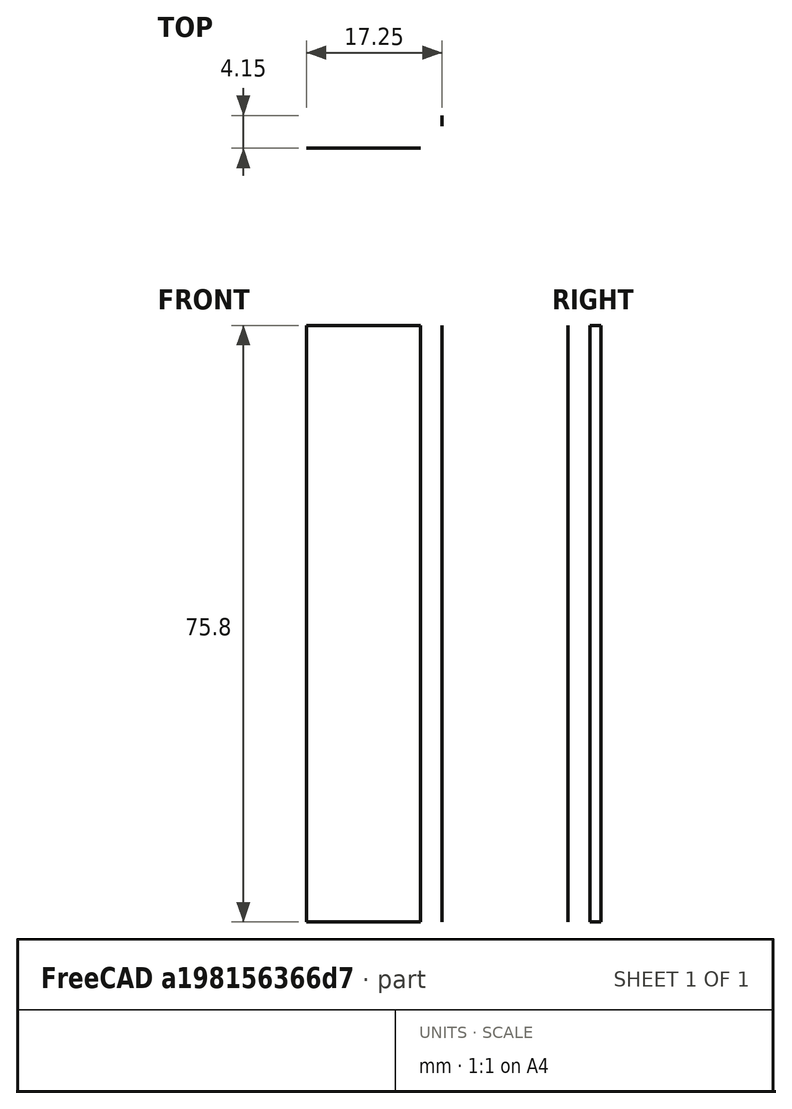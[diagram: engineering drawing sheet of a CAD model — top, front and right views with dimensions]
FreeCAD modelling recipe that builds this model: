
FCSTD DOCUMENT  (FreeCAD 2021.717R24301 +3842 (Git))
Label: Z-carriage
License: Creative Commons Attribution
LicenseURL: http://creativecommons.org/licenses/by/4.0/
objects: App::FeaturePython×34, Part::FeaturePython×25, App::Link×11
note: 24 computed .brp shape members not serialized (recipe doc carries the construction recipe); baked Part::Feature solids carry a one-line shape summary decoded from their .brp
EXTERNAL_REF file=parts/Spindle.FCStd obj=Assembly001
EXTERNAL_REF file=parts/HGH20CA.FCStd obj=Assembly
EXTERNAL_REF file=parts/HGH20CA.FCStd obj=Assembly001
EXTERNAL_REF file=parts/BallNut.FCStd obj=Assembly
EXTERNAL_REF file=parts/Z axis plates.FCStd obj=Assembly002
EXTERNAL_REF file=parts/Z axis plates.FCStd obj=Assembly001
EXTERNAL_REF file=parts/Z axis plates.FCStd obj=Assembly003
EXTERNAL_REF file=parts/Spindle.FCStd obj=Assembly002

FEATURE [App::Link] Link023  label="Spindle 0.8KW"
  AutoLinkLabel = true
  AutoPlacement = true
  LinkPlacement = pos=(255,-86.85,-102.5) rot=(0,0,-1;3.14159rad)
  LinkedObject = -> <external parts/Spindle.FCStd>#Assembly001
  Placement = pos=(255,-86.85,-102.5) rot=(0,0,-1;3.14159rad)
  SyncGroupVisibility = false
  _LinkVersion = 1
FEATURE [App::Link] Link003  label="HGH20CA-L-B"
  AutoLinkLabel = true
  AutoPlacement = true
  LinkPlacement = pos=(34,-18.45,-40.5) rot=(0,0.707107,-0.707107;3.14159rad)
  LinkedObject = -> <external parts/HGH20CA.FCStd>#Assembly
  Placement = pos=(34,-18.45,-40.5) rot=(0,0.707107,-0.707107;3.14159rad)
  SyncGroupVisibility = false
  _LinkVersion = 1
FEATURE [App::Link] Link004  label="HGH20CA-L-T"
  AutoLinkLabel = true
  AutoPlacement = true
  LinkPlacement = pos=(34,-18.45,40.5) rot=(0,0.707107,-0.707107;3.14159rad)
  LinkedObject = -> <external parts/HGH20CA.FCStd>#Assembly001
  Placement = pos=(34,-18.45,40.5) rot=(0,0.707107,-0.707107;3.14159rad)
  SyncGroupVisibility = false
  _LinkVersion = 1
FEATURE [App::Link] Link010  label="NUT"
  AutoLinkLabel = true
  AutoPlacement = true
  LinkPlacement = pos=(88,-43.45,-28.4) rot=(-1,0,0;1.5708rad)
  LinkedObject = -> <external parts/BallNut.FCStd>#Assembly
  Placement = pos=(88,-43.45,-28.4) rot=(-1,0,0;1.5708rad)
  SyncGroupVisibility = false
  _LinkVersion = 1
FEATURE [App::Link] Link013  label="Shim-L"
  AutoLinkLabel = true
  AutoPlacement = true
  LinkPlacement = pos=(88,-14.3,-9.24e-14) rot=(0,0,1;0rad)
  LinkedObject = -> <external parts/Z axis plates.FCStd>#Assembly002
  Placement = pos=(88,-14.3,-9.24e-14) rot=(0,0,1;0rad)
  SyncGroupVisibility = false
  _LinkVersion = 1
FEATURE [App::Link] Link014  label="Shim-R"
  AutoLinkLabel = true
  AutoPlacement = true
  LinkPlacement = pos=(88,-14.3,-1.705e-13) rot=(0,1,0;3.14159rad)
  LinkedObject = -> <external parts/Z axis plates.FCStd>#Assembly002
  Placement = pos=(88,-14.3,-1.705e-13) rot=(0,1,0;3.14159rad)
  SyncGroupVisibility = false
  _LinkVersion = 1
FEATURE [App::Link] Link015  label="Frontplate"
  AutoLinkLabel = true
  AutoPlacement = true
  LinkedObject = -> <external parts/Z axis plates.FCStd>#Assembly001
  SyncGroupVisibility = false
  _LinkVersion = 1
FEATURE [App::Link] Link016  label="Shim-Nut"
  AutoLinkLabel = true
  AutoPlacement = true
  LinkPlacement = pos=(216,-30.45,7.1e-15) rot=(0,0,1;0rad)
  LinkedObject = -> <external parts/Z axis plates.FCStd>#Assembly003
  Placement = pos=(216,-30.45,7.1e-15) rot=(0,0,1;0rad)
  SyncGroupVisibility = false
  _LinkVersion = 1
FEATURE [App::Link] Link  label="HGH20CA-R-T"
  AutoLinkLabel = true
  AutoPlacement = true
  LinkPlacement = pos=(142,-18.45,40.5) rot=(-1,0,0;4.71239rad)
  LinkedObject = -> Link003
  Placement = pos=(142,-18.45,40.5) rot=(-1,0,0;4.71239rad)
  SyncGroupVisibility = false
  _LinkVersion = 1
FEATURE [App::Link] Link024  label="HGH20CA-R-B"
  AutoLinkLabel = true
  AutoPlacement = true
  LinkPlacement = pos=(142,-18.45,-40.5) rot=(-1,0,0;4.71239rad)
  LinkedObject = -> Link004
  Placement = pos=(142,-18.45,-40.5) rot=(-1,0,0;4.71239rad)
  SyncGroupVisibility = false
  _LinkVersion = 1
FEATURE [App::Link] Link025  label="Makita router"
  AutoLinkLabel = true
  AutoPlacement = true
  LinkPlacement = pos=(-82,48.15,-102.5) rot=(0,0,-1;3.14159rad)
  LinkedObject = -> <external parts/Spindle.FCStd>#Assembly002
  Placement = pos=(-82,48.15,-102.5) rot=(0,0,-1;3.14159rad)
  SyncGroupVisibility = false
  _LinkVersion = 1
FEATURE [Part::FeaturePython] Parts  # WARN: FeaturePython — macro-defined, semantics opaque (R4)
  Group = -> [Link023,Link003,Link004,Link010,Link013,Link014,Link015,Link016,Link,Link024,Link025]
  GroupMode = 0
  _LinkVersion = 1
FEATURE [Part::FeaturePython] Assembly  label="Z carriage Assembly"  # WARN: FeaturePython — macro-defined, semantics opaque (R4)
  AutoRelax = true
  BuildShape = 0
  Freeze = false
  Group = -> [Constraints,Elements,Parts]
  Verbose = false
  _LinkVersion = 1
  _SolverType = 1
  _Version = 1
FEATURE [App::FeaturePython] Constraints  # WARN: FeaturePython — macro-defined, semantics opaque (R4)
  Group = -> [Constraint,Constraint001,Constraint002,Constraint003,Constraint004,Constraint005,Constraint006,Constraint007,Constraint008,Constraint009,Constraint010]
  _LinkVersion = 1
  _Version = 1
FEATURE [App::FeaturePython] Elements  # WARN: FeaturePython — macro-defined, semantics opaque (R4)
  Group = -> [_Element,_Element001,_Element002,_Element003,_Element004,_Element005,_Element006,_Element007,_Element008,_Element009,_Element010,_Element011,_Element012,_Element013,_Element014,_Element015,_Element016,_Element017,_Element018,Element,Element001,Element002,Element003]
  _LinkVersion = 1
FEATURE [App::FeaturePython] Constraint  label="Locked"  # WARN: FeaturePython — macro-defined, semantics opaque (R4)
  Disabled = false
  Group = -> [ElementLink]
  _ConstraintType = 0
  _LinkVersion = 1
  _Parent = -> Constraints
FEATURE [App::FeaturePython] ElementLink  label="shim-t-l@Frontplate-Assembly"  # link proxy (typed FeaturePython)
  LinkTransform = true
  LinkedObject = -> _Element
  _LinkVersion = 1
  _Parent = -> Constraint
FEATURE [Part::FeaturePython] _Element  label="shim-t-l@Frontplate-Assembly"  # link proxy (typed FeaturePython)
  Detach = false
  LinkTransform = true
  LinkedObject = -> Link015 [1.$shim-t-l.]
  _LinkVersion = 1
  _Parent = -> Elements
FEATURE [App::FeaturePython] Constraint001  label="Attachment-shim-left"  # WARN: FeaturePython — macro-defined, semantics opaque (R4)
  Cascade = false
  Disabled = false
  Group = -> [ElementLink001,ElementLink002]
  Multiply = false
  _ConstraintType = 45
  _LinkVersion = 1
  _Parent = -> Constraints
FEATURE [App::FeaturePython] ElementLink001  label="front-tl@Shim-Assembly"  # link proxy (typed FeaturePython)
  LinkTransform = true
  LinkedObject = -> _Element001
  Offset = pos=(0,0,0) rot=(1,0,0;3.14159rad)
  Placement = pos=(0,-128.3,117) rot=(1,0,0;3.14159rad)
  _LinkVersion = 1
  _Parent = -> Constraint001
FEATURE [Part::FeaturePython] _Element001  label="front-tl@Shim-Assembly"  # link proxy (typed FeaturePython)
  Detach = false
  LinkTransform = true
  LinkedObject = -> Link013 [1.$front-tl.]
  _LinkVersion = 1
  _Parent = -> Elements
FEATURE [App::FeaturePython] ElementLink002  label="shim-t-l@Frontplate-Assembly"  # link proxy (typed FeaturePython)
  LinkTransform = true
  LinkedObject = -> _Element
  _LinkVersion = 1
  _Parent = -> Constraint001
FEATURE [Part::FeaturePython] _Element002  label="shim-t-r@Frontplate-Assembly"  # link proxy (typed FeaturePython)
  Detach = false
  LinkTransform = true
  LinkedObject = -> Link015 [1.$shim-t-r.]
  _LinkVersion = 1
  _Parent = -> Elements
FEATURE [Part::FeaturePython] _Element003  label="front-tl@Shim-Assembly001"  # link proxy (typed FeaturePython)
  Detach = false
  LinkTransform = true
  LinkedObject = -> Link014 [1.$front-tl.]
  _LinkVersion = 1
  _Parent = -> Elements
FEATURE [App::FeaturePython] Constraint002  label="Attachment-shim-right"  # WARN: FeaturePython — macro-defined, semantics opaque (R4)
  Cascade = false
  Disabled = false
  Group = -> [ElementLink003,ElementLink004]
  Multiply = false
  _ConstraintType = 45
  _LinkVersion = 1
  _Parent = -> Constraints
FEATURE [App::FeaturePython] ElementLink003  label="front-bl@Shim-Assembly"  # link proxy (typed FeaturePython)
  LinkTransform = true
  LinkedObject = -> _Element004
  Offset = pos=(0,0,0) rot=(1,0,0;3.14159rad)
  Placement = pos=(0,-128.3,117) rot=(1,0,0;3.14159rad)
  _LinkVersion = 1
  _Parent = -> Constraint002
FEATURE [Part::FeaturePython] _Element004  label="front-bl@Shim-Assembly"  # link proxy (typed FeaturePython)
  Detach = false
  LinkTransform = true
  LinkedObject = -> Link014 [1.$front-bl.]
  _LinkVersion = 1
  _Parent = -> Elements
FEATURE [App::FeaturePython] ElementLink004  label="shim-t-r@Frontplate-Assembly"  # link proxy (typed FeaturePython)
  LinkTransform = true
  LinkedObject = -> _Element002
  Offset = pos=(0,0,0) rot=(0,0,1;3.14159rad)
  Placement = pos=(316,1.42e-14,117) rot=(0,1,0;3.14159rad)
  _LinkVersion = 1
  _Parent = -> Constraint002
FEATURE [App::FeaturePython] Constraint003  label="Attachment-shim"  # WARN: FeaturePython — macro-defined, semantics opaque (R4)
  Cascade = false
  Disabled = false
  Group = -> [ElementLink005,ElementLink006]
  Multiply = false
  _ConstraintType = 45
  _LinkVersion = 1
  _Parent = -> Constraints
FEATURE [App::FeaturePython] ElementLink005  label="fp-mate@Nut-shim-Assembly"  # link proxy (typed FeaturePython)
  LinkTransform = true
  LinkedObject = -> _Element005
  _LinkVersion = 1
  _Parent = -> Constraint003
FEATURE [Part::FeaturePython] _Element005  label="fp-mate@Nut-shim-Assembly"  # link proxy (typed FeaturePython)
  Detach = false
  LinkTransform = true
  LinkedObject = -> Link016 [1.$fp-mate.]
  _LinkVersion = 1
  _Parent = -> Elements
FEATURE [App::FeaturePython] ElementLink006  label="shim-nut-mate@Frontplate-Assembly"  # link proxy (typed FeaturePython)
  LinkTransform = true
  LinkedObject = -> _Element006
  _LinkVersion = 1
  _Parent = -> Constraint003
FEATURE [Part::FeaturePython] _Element006  label="shim-nut-mate@Frontplate-Assembly"  # link proxy (typed FeaturePython)
  Detach = false
  LinkTransform = true
  LinkedObject = -> Link015 [1.$shim-nut-mate.]
  _LinkVersion = 1
  _Parent = -> Elements
FEATURE [App::FeaturePython] Constraint004  label="Attachment-nut"  # WARN: FeaturePython — macro-defined, semantics opaque (R4)
  Cascade = false
  Disabled = false
  Group = -> [ElementLink007,ElementLink008]
  Multiply = false
  _ConstraintType = 45
  _LinkVersion = 1
  _Parent = -> Constraints
FEATURE [App::FeaturePython] ElementLink007  label="nut-mate@Nut-shim-Assembly"  # link proxy (typed FeaturePython)
  LinkTransform = true
  LinkedObject = -> _Element007
  _LinkVersion = 1
  _Parent = -> Constraint004
FEATURE [Part::FeaturePython] _Element007  label="nut-mate@Nut-shim-Assembly"  # link proxy (typed FeaturePython)
  Detach = false
  LinkTransform = true
  LinkedObject = -> Link016 [1.$nut-mate.]
  _LinkVersion = 1
  _Parent = -> Elements
FEATURE [App::FeaturePython] ElementLink008  label="shim-mate@NUT Assembly"  # link proxy (typed FeaturePython)
  LinkTransform = true
  LinkedObject = -> _Element008
  _LinkVersion = 1
  _Parent = -> Constraint004
FEATURE [Part::FeaturePython] _Element008  label="shim-mate@NUT Assembly"  # link proxy (typed FeaturePython)
  Detach = false
  LinkTransform = true
  LinkedObject = -> Link010 [1.$shim-mate.]
  _LinkVersion = 1
  _Parent = -> Elements
FEATURE [App::FeaturePython] Constraint005  label="Attachment-spindle"  # WARN: FeaturePython — macro-defined, semantics opaque (R4)
  Cascade = false
  Disabled = false
  Group = -> [ElementLink009,ElementLink010]
  Multiply = false
  _ConstraintType = 45
  _LinkVersion = 1
  _Parent = -> Constraints
FEATURE [App::FeaturePython] ElementLink009  label="FP-mate-tl@0_8KW spindle Assembly"  # link proxy (typed FeaturePython)
  LinkTransform = true
  LinkedObject = -> _Element009
  _LinkVersion = 1
  _Parent = -> Constraint005
FEATURE [Part::FeaturePython] _Element009  label="FP-mate-tl@0_8KW spindle Assembly"  # link proxy (typed FeaturePython)
  Detach = false
  LinkTransform = true
  LinkedObject = -> Link023 [1.$FP-mate-tl.]
  _LinkVersion = 1
  _Parent = -> Elements
FEATURE [App::FeaturePython] ElementLink010  label="spindle-65mm-tl@Frontplate-Assembly"  # link proxy (typed FeaturePython)
  LinkTransform = true
  LinkedObject = -> _Element010
  _LinkVersion = 1
  _Parent = -> Constraint005
FEATURE [Part::FeaturePython] _Element010  label="spindle-65mm-tl@Frontplate-Assembly"  # link proxy (typed FeaturePython)
  Detach = false
  LinkTransform = true
  LinkedObject = -> Link015 [1.$spindle-65mm-tl.]
  _LinkVersion = 1
  _Parent = -> Elements
FEATURE [App::FeaturePython] Constraint006  label="Attachment-cart-tl"  # WARN: FeaturePython — macro-defined, semantics opaque (R4)
  Cascade = false
  Disabled = false
  Group = -> [ElementLink011,ElementLink012]
  Multiply = false
  _ConstraintType = 45
  _LinkVersion = 1
  _Parent = -> Constraints
FEATURE [App::FeaturePython] ElementLink011  label="shim-br@HGH20CA-R-Assembly"  # link proxy (typed FeaturePython)
  LinkTransform = true
  LinkedObject = -> _Element011
  _LinkVersion = 1
  _Parent = -> Constraint006
FEATURE [Part::FeaturePython] _Element011  label="shim-br@HGH20CA-R-Assembly"  # link proxy (typed FeaturePython)
  Detach = false
  LinkTransform = true
  LinkedObject = -> Link004 [1.$shim-br.]
  _LinkVersion = 1
  _Parent = -> Elements
FEATURE [App::FeaturePython] ElementLink012  label="cart-tl@Shim-Assembly"  # link proxy (typed FeaturePython)
  LinkTransform = true
  LinkedObject = -> _Element012
  _LinkVersion = 1
  _Parent = -> Constraint006
FEATURE [Part::FeaturePython] _Element012  label="cart-tl@Shim-Assembly"  # link proxy (typed FeaturePython)
  Detach = false
  LinkTransform = true
  LinkedObject = -> Link013 [1.$cart-tl.]
  _LinkVersion = 1
  _Parent = -> Elements
FEATURE [App::FeaturePython] Constraint007  label="Attachment-cart-bl"  # WARN: FeaturePython — macro-defined, semantics opaque (R4)
  Cascade = false
  Disabled = false
  Group = -> [ElementLink013,ElementLink014]
  Multiply = false
  _ConstraintType = 45
  _LinkVersion = 1
  _Parent = -> Constraints
FEATURE [App::FeaturePython] ElementLink013  label="shim-tr@HGH20CA-L-Assembly"  # link proxy (typed FeaturePython)
  LinkTransform = true
  LinkedObject = -> _Element013
  _LinkVersion = 1
  _Parent = -> Constraint007
FEATURE [Part::FeaturePython] _Element013  label="shim-tr@HGH20CA-L-Assembly"  # link proxy (typed FeaturePython)
  Detach = false
  LinkTransform = true
  LinkedObject = -> Link003 [1.$shim-tr.]
  _LinkVersion = 1
  _Parent = -> Elements
FEATURE [App::FeaturePython] ElementLink014  label="cart-bl@Shim-Assembly"  # link proxy (typed FeaturePython)
  LinkTransform = true
  LinkedObject = -> _Element014
  _LinkVersion = 1
  _Parent = -> Constraint007
FEATURE [Part::FeaturePython] _Element014  label="cart-bl@Shim-Assembly"  # link proxy (typed FeaturePython)
  Detach = false
  LinkTransform = true
  LinkedObject = -> Link013 [1.$cart-bl.]
  _LinkVersion = 1
  _Parent = -> Elements
FEATURE [Part::FeaturePython] _Element015  label="shim-tr@HGH20CA-L-Assembly001"  # link proxy (typed FeaturePython)
  Detach = false
  LinkTransform = true
  LinkedObject = -> Link [1.$shim-tr.]
  _LinkVersion = 1
  _Parent = -> Elements
FEATURE [App::FeaturePython] Constraint008  label="Attachment-cart-tr"  # WARN: FeaturePython — macro-defined, semantics opaque (R4)
  Cascade = false
  Disabled = false
  Group = -> [ElementLink015,ElementLink016]
  Multiply = false
  _ConstraintType = 45
  _LinkVersion = 1
  _Parent = -> Constraints
FEATURE [App::FeaturePython] ElementLink015  label="shim-tr@HGH20CA-L-Assembly001"  # link proxy (typed FeaturePython)
  LinkTransform = true
  LinkedObject = -> _Element015
  _LinkVersion = 1
  _Parent = -> Constraint008
FEATURE [App::FeaturePython] ElementLink016  label="cart-bl@Shim-Assembly001"  # link proxy (typed FeaturePython)
  LinkTransform = true
  LinkedObject = -> _Element016
  _LinkVersion = 1
  _Parent = -> Constraint008
FEATURE [Part::FeaturePython] _Element016  label="cart-bl@Shim-Assembly001"  # link proxy (typed FeaturePython)
  Detach = false
  LinkTransform = true
  LinkedObject = -> Link014 [1.$cart-bl.]
  _LinkVersion = 1
  _Parent = -> Elements
FEATURE [App::FeaturePython] Constraint009  label="Attachment-cart-br"  # WARN: FeaturePython — macro-defined, semantics opaque (R4)
  Cascade = false
  Disabled = false
  Group = -> [ElementLink017,ElementLink018]
  Multiply = false
  _ConstraintType = 45
  _LinkVersion = 1
  _Parent = -> Constraints
FEATURE [App::FeaturePython] ElementLink017  label="cart-tl@Shim-Assembly001"  # link proxy (typed FeaturePython)
  LinkTransform = true
  LinkedObject = -> _Element017
  _LinkVersion = 1
  _Parent = -> Constraint009
FEATURE [Part::FeaturePython] _Element017  label="cart-tl@Shim-Assembly001"  # link proxy (typed FeaturePython)
  Detach = false
  LinkTransform = true
  LinkedObject = -> Link014 [1.$cart-tl.]
  _LinkVersion = 1
  _Parent = -> Elements
FEATURE [App::FeaturePython] ElementLink018  label="shim-br@HGH20CA-R-Assembly001"  # link proxy (typed FeaturePython)
  LinkTransform = true
  LinkedObject = -> _Element018
  _LinkVersion = 1
  _Parent = -> Constraint009
FEATURE [Part::FeaturePython] _Element018  label="shim-br@HGH20CA-R-Assembly001"  # link proxy (typed FeaturePython)
  Detach = false
  LinkTransform = true
  LinkedObject = -> Link024 [1.$shim-br.]
  _LinkVersion = 1
  _Parent = -> Elements
FEATURE [Part::FeaturePython] Element  label="point@HGH20CA-R-Assembly"  # link proxy (typed FeaturePython)
  Detach = false
  LinkTransform = true
  LinkedObject = -> Link024 [1.$point.]
  _LinkVersion = 1
  _Parent = -> Elements
FEATURE [Part::FeaturePython] Element001  label="top-mate@HGH20CA-R-Assembly"  # link proxy (typed FeaturePython)
  Detach = false
  LinkTransform = true
  LinkedObject = -> Link024 [1.$top-mate.]
  _LinkVersion = 1
  _Parent = -> Elements
FEATURE [Part::FeaturePython] Element002  label="side-mate@HGH20CA-R-Assembly"  # link proxy (typed FeaturePython)
  Detach = false
  LinkTransform = true
  LinkedObject = -> Link024 [1.$side-mate.]
  _LinkVersion = 1
  _Parent = -> Elements
FEATURE [Part::FeaturePython] Element003  label="FP-mate@Makita router Assembly"  # link proxy (typed FeaturePython)
  Detach = false
  LinkTransform = true
  LinkedObject = -> Link025 [1.$FP-mate.]
  _LinkVersion = 1
  _Parent = -> Elements
FEATURE [App::FeaturePython] Constraint010  label="Attachment"  # WARN: FeaturePython — macro-defined, semantics opaque (R4)
  Cascade = false
  Disabled = false
  Group = -> [ElementLink019,ElementLink020]
  Multiply = false
  _ConstraintType = 45
  _LinkVersion = 1
  _Parent = -> Constraints
FEATURE [App::FeaturePython] ElementLink019  label="spindle-65mm-tl@Frontplate-Assembly"  # link proxy (typed FeaturePython)
  LinkTransform = true
  LinkedObject = -> _Element010
  _LinkVersion = 1
  _Parent = -> Constraint010
FEATURE [App::FeaturePython] ElementLink020  label="FP-mate@Makita router Assembly"  # link proxy (typed FeaturePython)
  LinkTransform = true
  LinkedObject = -> Element003
  _LinkVersion = 1
  _Parent = -> Constraint010

RESOLVED EXTERNAL PARTS (link-assembly join: the EXTERNAL_REF files above that resolve inside this repo's crawl, each included once):
---- part parts/BallNut.FCStd = doc fcstd_aec63517059e ----
FCSTD DOCUMENT  (FreeCAD 2021.614R24301 +3747 (Git))
Label: BallNut
License: Creative Commons Attribution
LicenseURL: http://creativecommons.org/licenses/by/4.0/
objects: App::FeaturePython×25, Part::FeaturePython×22, Sketcher::SketchObject×9, PartDesign::Pocket×6, App::LinkElement×6, PartDesign::Pad×3, App::Link×3, PartDesign::Chamfer×2, PartDesign::Body×2, PartDesign::Plane×1, PartDesign::Line×1, App::DocumentObjectGroup×1
note: 67 computed .brp shape members not serialized (recipe doc carries the construction recipe); baked Part::Feature solids carry a one-line shape summary decoded from their .brp

FEATURE [Sketcher::SketchObject] Sketch
  FullyConstrained = true
  MapMode = 5
  Placement = pos=(0,0,0) rot=(1,0,0;1.5708rad)
  Support = -> [XZ_Plane]
  sketch-geometry (9):
    g0: Circle CenterX=0 CenterY=0 CenterZ=0 NormalX=0 NormalY=0 NormalZ=1 AngleXU=0 Radius=14
    g1: LineSegment StartX=-26.125 StartY=-20 StartZ=0 EndX=26.125 EndY=-20 EndZ=0
    g2: LineSegment StartX=26.125 StartY=-20 StartZ=0 EndX=26.125 EndY=8 EndZ=0
    g3: LineSegment StartX=26.125 StartY=8 StartZ=0 EndX=14 EndY=20 EndZ=0
    g4: LineSegment StartX=14 StartY=20 StartZ=0 EndX=-14 EndY=20 EndZ=0
    g5: LineSegment StartX=-14 StartY=20 StartZ=0 EndX=-26.125 EndY=8 EndZ=0
    g6: LineSegment StartX=-26.125 StartY=8 StartZ=0 EndX=-26.125 EndY=-20 EndZ=0
    g7: GeomPoint [constr] X=0 Y=-20 Z=0
    g8: GeomPoint [constr] X=2e-16 Y=20 Z=0
  constraints (21):
    c: Coincident(g0,g-1)
    c: Horizontal(g1)
    c: Coincident(g1,g2)
    c: Vertical(g2)
    c: Coincident(g2,g3)
    c: Coincident(g3,g4)
    c: Horizontal(g4)
    c: Coincident(g4,g5)
    c: Coincident(g5,g6)
    c: Coincident(g6,g1)
    c: Vertical(g6)
    c: Horizontal(g5,g2)
    c: PointOnObject(g7,g-2)
    c: Symmetric(g4,g3,g8)
    c: Symmetric(g1,g1,g7)
    c: DistanceY(g1,g3) = 40
    c: Symmetric(g8,g7,g0)
    c: DistanceX(g1,g1) = 52.25
    c: DistanceY(g2,g2) = 28
    c: DistanceX(g4,g4) = 28
    c: Diameter(g0) = 28
FEATURE [PartDesign::Pad] Pad
  ClaimChildren = false
  Direction = (1,1,1)
  Fit = 0
  FitJoin = 0
  InnerFit = 0
  InnerFitJoin = 0
  InnerTaperAngle = 0
  InnerTaperAngleRev = 0
  Length = 40.25
  Length2 = 100
  Linearize = true
  Midplane = true
  NewSolid = false
  Placement = pos=(0,0,0) rot=(1,0,0;1.5708rad)
  Profile = -> Sketch
  Refine = true
  Suppress = false
  Type = 0
FEATURE [Sketcher::SketchObject] Sketch001
  FullyConstrained = true
  MapMode = 5
  Placement = pos=(0,-20.125,4.4e-15) rot=(1,0,0;1.5708rad)
  Support = -> [Pad]
  sketch-geometry (8):
    g0: Circle CenterX=-19 CenterY=0 CenterZ=0 NormalX=0 NormalY=0 NormalZ=1 AngleXU=0 Radius=2.1
    g1: Circle CenterX=19 CenterY=0 CenterZ=0 NormalX=0 NormalY=0 NormalZ=1 AngleXU=0 Radius=2.1
    g2: Circle CenterX=13.435 CenterY=-13.435 CenterZ=0 NormalX=0 NormalY=0 NormalZ=1 AngleXU=0 Radius=2.1
    g3: Circle CenterX=-13.435 CenterY=-13.435 CenterZ=0 NormalX=0 NormalY=0 NormalZ=1 AngleXU=0 Radius=2.1
    g4: Circle CenterX=-13.435 CenterY=13.435 CenterZ=0 NormalX=0 NormalY=0 NormalZ=1 AngleXU=0 Radius=2.1
    g5: Circle CenterX=13.435 CenterY=13.435 CenterZ=0 NormalX=0 NormalY=0 NormalZ=1 AngleXU=0 Radius=2.1
    g6: Circle [constr] CenterX=0 CenterY=0 CenterZ=0 NormalX=0 NormalY=0 NormalZ=1 AngleXU=0 Radius=19
    g7: LineSegment [constr] StartX=0 StartY=0 StartZ=0 EndX=13.435 EndY=13.435 EndZ=0
  constraints (22):
    c: PointOnObject(g0,g-1)
    c: PointOnObject(g1,g-1)
    c: Coincident(g6,g-1)
    c: Diameter(g6) = 38
    c: Equal(g1,g5)
    c: Equal(g5,g4)
    c: Equal(g4,g0)
    c: Equal(g0,g3)
    c: Equal(g3,g2)
    c: PointOnObject(g5,g6)
    c: PointOnObject(g4,g6)
    c: PointOnObject(g0,g6)
    c: PointOnObject(g1,g6)
    c: PointOnObject(g2,g6)
    c: PointOnObject(g3,g6)
    c: Vertical(g4,g3)
    c: Vertical(g5,g2)
    c: Horizontal(g4,g5)
    c: Diameter(g4) = 4.2
    c: Coincident(g7,g6)
    c: Coincident(g7,g5)
    c: Angle(g-1,g7) = 0.785398
FEATURE [PartDesign::Pocket] Pocket
  BaseFeature = -> Pad
  ClaimChildren = false
  Fit = 0
  FitJoin = 0
  InnerFit = 0
  InnerFitJoin = 0
  InnerTaperAngle = 0
  InnerTaperAngleRev = 0
  Length = 16
  Length2 = 100
  Linearize = true
  NewSolid = false
  Placement = pos=(0,0,0) rot=(1,0,0;1.5708rad)
  Profile = -> Sketch001
  Refine = true
  Suppress = false
  Type = 0
FEATURE [Sketcher::SketchObject] Sketch002
  FullyConstrained = true
  MapMode = 5
  Placement = pos=(0,-8.8e-15,-20) rot=(1,0,0;3.14159rad)
  Support = -> [Pocket]
  sketch-geometry (4):
    g0: Circle CenterX=-20 CenterY=12 CenterZ=0 NormalX=0 NormalY=0 NormalZ=1 AngleXU=0 Radius=2.1
    g1: Circle CenterX=20 CenterY=12 CenterZ=0 NormalX=0 NormalY=0 NormalZ=1 AngleXU=0 Radius=2.1
    g2: Circle CenterX=-20 CenterY=-12 CenterZ=0 NormalX=0 NormalY=0 NormalZ=1 AngleXU=0 Radius=2.1
    g3: Circle CenterX=20 CenterY=-12 CenterZ=0 NormalX=0 NormalY=0 NormalZ=1 AngleXU=0 Radius=2.1
  constraints (11):
    c: Equal(g3,g1)
    c: Equal(g1,g0)
    c: Equal(g0,g2)
    c: Diameter(g0) = 4.2
    c: Symmetric(g0,g3,g-1)
    c: Horizontal(g0,g1)
    c: Vertical(g0,g2)
    c: Vertical(g1,g3)
    c: Horizontal(g3,g2)
    c: DistanceY(g2,g0) = 24
    c: DistanceX(g0,g1) = 40
FEATURE [PartDesign::Pocket] Pocket001
  BaseFeature = -> Pocket
  ClaimChildren = false
  Fit = 0
  FitJoin = 0
  InnerFit = 0
  InnerFitJoin = 0
  InnerTaperAngle = 0
  InnerTaperAngleRev = 0
  Length = 16
  Length2 = 100
  Linearize = true
  NewSolid = false
  Placement = pos=(0,0,0) rot=(1,0,0;1.5708rad)
  Profile = -> Sketch002
  Refine = true
  Suppress = false
  Type = 0
FEATURE [PartDesign::Chamfer] Chamfer
  Angle = 45
  Base = -> Pocket001 [Edge10,Edge2,Edge15,Edge14,Edge13,Edge12,Edge37,Edge9,Edge1,Edge4,Edge28,Edge38,Edge16,Edge3,Edge17,Edge19,Edge20,Edge18,Edge11,Edge25,Edge22,Edge21,Edge24,Edge26,Edge27,Edge23,Edge5,Edge7,Edge8,Edge6]
  BaseFeature = -> Pocket001
  ChamferType = 0
  FlipDirection = false
  NewSolid = false
  Placement = pos=(0,0,0) rot=(1,0,0;1.5708rad)
  Refine = true
  Size = 1
  Size2 = 1
  SupportTransform = false
  Suppress = false
FEATURE [Sketcher::SketchObject] Sketch003
  FullyConstrained = true
  MapMode = 5
  Placement = pos=(0,0,0) rot=(1,0,0;1.5708rad)
  Support = -> [XZ_Plane001]
  sketch-geometry (1):
    g0: Circle CenterX=0 CenterY=0 CenterZ=0 NormalX=0 NormalY=0 NormalZ=1 AngleXU=0 Radius=14
  constraints (2):
    c: Coincident(g0,g-1)
    c: Diameter(g0) = 28
FEATURE [PartDesign::Pad] Pad001
  ClaimChildren = false
  Direction = (1,1,1)
  Fit = 0
  FitJoin = 0
  InnerFit = 0
  InnerFitJoin = 0
  InnerTaperAngle = 0
  InnerTaperAngleRev = 0
  Length = 32
  Length2 = 100
  Linearize = true
  Midplane = true
  NewSolid = false
  Placement = pos=(0,0,0) rot=(1,0,0;1.5708rad)
  Profile = -> Sketch003
  Refine = true
  Suppress = false
  Type = 0
FEATURE [Sketcher::SketchObject] Sketch004
  FullyConstrained = true
  MapMode = 5
  Placement = pos=(0,-16,3.5e-15) rot=(1,0,0;1.5708rad)
  Support = -> [Pad001]
  sketch-geometry (12):
    g0: ArcOfCircle CenterX=0 CenterY=0 CenterZ=0 NormalX=0 NormalY=0 NormalZ=1 AngleXU=0 Radius=24 StartAngle=2.15648 EndAngle=4.1267
    g1: Circle [constr] CenterX=0 CenterY=0 CenterZ=0 NormalX=0 NormalY=0 NormalZ=1 AngleXU=0 Radius=19
    g2: LineSegment StartX=-13.2665 StartY=20 StartZ=0 EndX=13.2665 EndY=20 EndZ=0
    g3: LineSegment StartX=-13.2665 StartY=-20 StartZ=0 EndX=13.2665 EndY=-20 EndZ=0
    g4: ArcOfCircle CenterX=0 CenterY=0 CenterZ=0 NormalX=0 NormalY=0 NormalZ=1 AngleXU=0 Radius=24 StartAngle=5.29807 EndAngle=7.2683
    g5: Circle CenterX=-19 CenterY=0 CenterZ=0 NormalX=0 NormalY=0 NormalZ=1 AngleXU=0 Radius=2.75
    g6: Circle CenterX=-13.435 CenterY=13.435 CenterZ=0 NormalX=0 NormalY=0 NormalZ=1 AngleXU=0 Radius=2.75
    g7: Circle CenterX=13.435 CenterY=13.435 CenterZ=0 NormalX=0 NormalY=0 NormalZ=1 AngleXU=0 Radius=2.75
    g8: Circle CenterX=19 CenterY=0 CenterZ=0 NormalX=0 NormalY=0 NormalZ=1 AngleXU=0 Radius=2.75
    g9: Circle CenterX=13.435 CenterY=-13.435 CenterZ=0 NormalX=0 NormalY=0 NormalZ=1 AngleXU=0 Radius=2.75
    g10: Circle CenterX=-13.435 CenterY=-13.435 CenterZ=0 NormalX=0 NormalY=0 NormalZ=1 AngleXU=0 Radius=2.75
    g11: LineSegment [constr] StartX=0 StartY=0 StartZ=0 EndX=13.435 EndY=13.435 EndZ=0
  constraints (34):
    c: Coincident(g0,g-1)
    c: Coincident(g1,g0)
    c: Diameter(g1) = 38
    c: Diameter(g0) = 48
    c: Horizontal(g2)
    c: Horizontal(g3)
    c: Symmetric(g3,g2,g0)
    c: DistanceY(g3,g2) = 40
    c: Coincident(g0,g2)
    c: Coincident(g4,g2)
    c: Equal(g0,g4)
    c: Coincident(g0,g3)
    c: PointOnObject(g4,g3)
    c: Coincident(g0,g4)
    c: PointOnObject(g5,g1)
    c: PointOnObject(g6,g1)
    c: PointOnObject(g7,g1)
    c: PointOnObject(g8,g1)
    c: PointOnObject(g9,g1)
    c: PointOnObject(g8,g-1)
    c: PointOnObject(g5,g-1)
    c: PointOnObject(g10,g1)
    c: Vertical(g10,g6)
    c: Vertical(g7,g9)
    c: Horizontal(g7,g6)
    c: Equal(g7,g8)
    c: Equal(g8,g9)
    c: Equal(g9,g6)
    c: Equal(g6,g5)
    c: Equal(g5,g10)
    c: Diameter(g6) = 5.5
    c: Coincident(g11,g0)
    c: Coincident(g11,g7)
    c: Angle(g-1,g11) = 0.785398
FEATURE [PartDesign::Pad] Pad002
  BaseFeature = -> Pad001
  ClaimChildren = false
  Direction = (1,1,1)
  Fit = 0
  FitJoin = 0
  InnerFit = 0
  InnerFitJoin = 0
  InnerTaperAngle = 0
  InnerTaperAngleRev = 0
  Length = 10
  Length2 = 100
  Linearize = true
  NewSolid = false
  Placement = pos=(0,0,0) rot=(1,0,0;1.5708rad)
  Profile = -> Sketch004
  Refine = true
  Suppress = false
  Type = 0
FEATURE [Sketcher::SketchObject] Sketch005
  FullyConstrained = true
  MapMode = 5
  Placement = pos=(0,-26,2.03e-14) rot=(1,0,0;1.5708rad)
  Support = -> [Pad002]
  sketch-geometry (1):
    g0: Circle CenterX=0 CenterY=0 CenterZ=0 NormalX=0 NormalY=0 NormalZ=1 AngleXU=0 Radius=8
  constraints (2):
    c: Coincident(g0,g-1)
    c: Diameter(g0) = 16
FEATURE [PartDesign::Pocket] Pocket002
  BaseFeature = -> Pad002
  ClaimChildren = false
  Fit = 0
  FitJoin = 0
  InnerFit = 0
  InnerFitJoin = 0
  InnerTaperAngle = 0
  InnerTaperAngleRev = 0
  Length = 5
  Length2 = 100
  Linearize = true
  NewSolid = false
  Placement = pos=(0,0,0) rot=(1,0,0;1.5708rad)
  Profile = -> Sketch005
  Refine = true
  Suppress = false
  Type = 1
FEATURE [Sketcher::SketchObject] Sketch006
  FullyConstrained = true
  MapMode = 5
  Placement = pos=(0,-26,2.03e-14) rot=(1,0,0;1.5708rad)
  Support = -> [Pocket002]
  sketch-geometry (1):
    g0: Circle CenterX=0 CenterY=0 CenterZ=0 NormalX=0 NormalY=0 NormalZ=1 AngleXU=0 Radius=11
  constraints (2):
    c: Coincident(g0,g-1)
    c: Diameter(g0) = 22
FEATURE [PartDesign::Pocket] Pocket003
  BaseFeature = -> Pocket002
  ClaimChildren = false
  Fit = 0
  FitJoin = 0
  InnerFit = 0
  InnerFitJoin = 0
  InnerTaperAngle = 0
  InnerTaperAngleRev = 0
  Length = 1
  Length2 = 100
  Linearize = true
  NewSolid = false
  Placement = pos=(0,0,0) rot=(1,0,0;1.5708rad)
  Profile = -> Sketch006
  Refine = true
  Suppress = false
  Type = 0
FEATURE [Sketcher::SketchObject] Sketch007
  FullyConstrained = true
  MapMode = 5
  Placement = pos=(0,16,-3.5e-15) rot=(-1,0,0;1.5708rad)
  Support = -> [Pocket003]
  sketch-geometry (1):
    g0: Circle CenterX=0 CenterY=0 CenterZ=0 NormalX=0 NormalY=0 NormalZ=1 AngleXU=0 Radius=11
  constraints (2):
    c: Coincident(g0,g-1)
    c: Diameter(g0) = 22
FEATURE [PartDesign::Pocket] Pocket004
  BaseFeature = -> Pocket003
  ClaimChildren = false
  Fit = 0
  FitJoin = 0
  InnerFit = 0
  InnerFitJoin = 0
  InnerTaperAngle = 0
  InnerTaperAngleRev = 0
  Length = 1
  Length2 = 100
  Linearize = true
  NewSolid = false
  Placement = pos=(0,0,0) rot=(1,0,0;1.5708rad)
  Profile = -> Sketch007
  Refine = true
  Suppress = false
  Type = 0
FEATURE [PartDesign::Plane] DatumPlane
  AttachmentOffset = pos=(0,0,0) rot=(1,0,0;0.392699rad)
  Length = 42
  MapMode = 5
  MinimumLength = 10
  MinimumWidth = 10
  Placement = pos=(0,0,0) rot=(0.639338,0.639338,0.427192;2.33414rad)
  ResizeMode = 0
  Support = -> [YZ_Plane001]
  Width = 55.324
FEATURE [Sketcher::SketchObject] Sketch008
  ExternalGeometry = -> [Pocket004]
  FullyConstrained = true
  MapMode = 5
  Placement = pos=(0,0,0) rot=(0.485653,-0.485653,-0.726831;1.88458rad)
  Support = -> [DatumPlane]
  sketch-geometry (3):
    g0: Circle CenterX=21 CenterY=0 CenterZ=0 NormalX=0 NormalY=0 NormalZ=1 AngleXU=0 Radius=2.5
    g1: LineSegment [constr] StartX=16 StartY=13.4007 StartZ=0 EndX=21 EndY=0 EndZ=0
    g2: LineSegment [constr] StartX=21 StartY=0 StartZ=0 EndX=26 EndY=13.4007 EndZ=0
  constraints (7):
    c: PointOnObject(g0,g-1)
    c: Coincident(g1,g-3)
    c: Coincident(g1,g0)
    c: Coincident(g2,g0)
    c: Coincident(g2,g-4)
    c: Equal(g2,g1)
    c: Diameter(g0) = 5
FEATURE [PartDesign::Pocket] Pocket005
  BaseFeature = -> Pocket004
  ClaimChildren = false
  Fit = 0
  FitJoin = 0
  InnerFit = 0
  InnerFitJoin = 0
  InnerTaperAngle = 0
  InnerTaperAngleRev = 0
  Length = 5
  Length2 = 100
  Linearize = true
  NewSolid = false
  Placement = pos=(0,0,0) rot=(1,0,0;1.5708rad)
  Profile = -> Sketch008
  Refine = true
  Reversed = true
  Suppress = false
  Type = 1
FEATURE [PartDesign::Chamfer] Chamfer001
  Angle = 45
  Base = -> Pocket005 [Edge35,Edge43,Edge24,Edge25,Edge26,Edge22,Edge21,Edge20,Edge23,Edge14,Edge16,Edge17,Edge11,Edge12,Edge13]
  BaseFeature = -> Pocket005
  ChamferType = 0
  FlipDirection = false
  NewSolid = false
  Placement = pos=(0,0,0) rot=(1,0,0;1.5708rad)
  Refine = true
  Size = 0.5
  Size2 = 1
  SupportTransform = false
  Suppress = false
FEATURE [PartDesign::Body] Body001  label="SFU1605"
  AutoGroupSolids = false
  ExportMode = 0
  Group = -> [Sketch003,Pad001,Sketch004,Pad002,Sketch005,Pocket002,Sketch006,Pocket003,Sketch007,Pocket004,DatumPlane,Sketch008,Pocket005,Chamfer001]
  Origin = -> Origin001
  Placement = pos=(0,-5,0) rot=(0,0,1;0rad)
  Tip = -> Chamfer001
  _ExportChildren = -> [Pad001,Pad002,Pocket002,Pocket003,Pocket004,DatumPlane,Pocket005,Chamfer001]
  _GroupVersion = 1
FEATURE [App::Link] Link  label="Link(SFU1605)"
  AutoLinkLabel = true
  LinkPlacement = pos=(4e-16,-5,-2.7e-15) rot=(0,0,1;0rad)
  LinkedObject = -> Body001
  Placement = pos=(4e-16,-5,-2.7e-15) rot=(0,0,1;0rad)
  SyncGroupVisibility = false
  _LinkVersion = 1
FEATURE [App::Link] Link001  label="Link001(DSG16)"
  AutoLinkLabel = true
  LinkPlacement = pos=(0,-0.875,-9.7e-15) rot=(0,0,1;0rad)
  LinkedObject = -> Body
  Placement = pos=(0,-0.875,-9.7e-15) rot=(0,0,1;0rad)
  SyncGroupVisibility = false
  _LinkVersion = 1
FEATURE [PartDesign::Line] DatumLine
  AttacherType = Attacher::AttachEngineLine
  Length = 40.25
  MapMode = 19
  MinimumLength = 10
  Placement = pos=(0,-19.125,4e-15) rot=(1,0,0;1.5708rad)
  ResizeMode = 0
  Support = -> [Chamfer]
FEATURE [PartDesign::Body] Body  label="DSG16"
  AutoGroupSolids = false
  ExportMode = 0
  Group = -> [Sketch,Pad,Sketch001,Pocket,Sketch002,Pocket001,Chamfer,DatumLine]
  Origin = -> Origin
  Tip = -> Chamfer
  _ExportChildren = -> [Pad,Pocket,Pocket001,Chamfer,DatumLine]
  _GroupVersion = 1
FEATURE [Part::FeaturePython] Screw  label="M5x20-Screw"  # Fasteners workbench fastener (typed FeaturePython)
  Placement = pos=(0,-51,0) rot=(0,0,1;0rad)
  diameter = 3
  invert = false
  length = 5
  lengthCustom = 20
  matchOuter = false
  offset = 0
  thread = false
  type = 39
FEATURE [App::DocumentObjectGroup] Group  label="Components"
  ExportMode = 1
  Group = -> [Body,Body001,Screw]
  _GroupVersion = 1
FEATURE [App::LinkElement] Link002_i0
  LinkPlacement = pos=(-13.435,20,13.435) rot=(1,0,0;1.5708rad)
  LinkedObject = -> Screw
  Placement = pos=(-13.435,20,13.435) rot=(1,0,0;1.5708rad)
  _LinkVersion = 0
FEATURE [App::LinkElement] Link002_i1
  LinkPlacement = pos=(13.435,20,13.435) rot=(1,0,0;1.5708rad)
  LinkedObject = -> Screw
  Placement = pos=(13.435,20,13.435) rot=(1,0,0;1.5708rad)
  _LinkVersion = 0
FEATURE [App::LinkElement] Link002_i2
  LinkPlacement = pos=(19,20,6.78e-14) rot=(1,0,0;1.5708rad)
  LinkedObject = -> Screw
  Placement = pos=(19,20,6.78e-14) rot=(1,0,0;1.5708rad)
  _LinkVersion = 0
FEATURE [App::LinkElement] Link002_i3
  LinkPlacement = pos=(13.435,20,-13.435) rot=(1,0,0;1.5708rad)
  LinkedObject = -> Screw
  Placement = pos=(13.435,20,-13.435) rot=(1,0,0;1.5708rad)
  _LinkVersion = 0
FEATURE [App::LinkElement] Link002_i4
  LinkPlacement = pos=(-19,20,6.78e-14) rot=(1,0,0;1.5708rad)
  LinkedObject = -> Screw
  Placement = pos=(-19,20,6.78e-14) rot=(1,0,0;1.5708rad)
  _LinkVersion = 0
FEATURE [App::LinkElement] Link002_i5
  LinkPlacement = pos=(-13.435,20,-13.435) rot=(1,0,0;1.5708rad)
  LinkedObject = -> Screw
  Placement = pos=(-13.435,20,-13.435) rot=(1,0,0;1.5708rad)
  _LinkVersion = 0
FEATURE [App::Link] Link002  label="M5x20-Screw 6ct"
  AutoLinkLabel = true
  ElementCount = 6
  ElementList = -> [Link002_i0,Link002_i1,Link002_i2,Link002_i3,Link002_i4,Link002_i5]
  LinkPlacement = pos=(0,-51,0) rot=(0,0,1;0rad)
  LinkedObject = -> Screw
  Placement = pos=(0,-51,0) rot=(0,0,1;0rad)
  SyncGroupVisibility = false
  _LinkVersion = 1
FEATURE [Part::FeaturePython] Parts  # WARN: FeaturePython — macro-defined, semantics opaque (R4)
  Group = -> [Link,Link001,Link002]
  GroupMode = 0
  _LinkVersion = 1
FEATURE [Part::FeaturePython] Assembly  label="NUT Assembly"  # WARN: FeaturePython — macro-defined, semantics opaque (R4)
  AutoRelax = true
  BuildShape = 0
  Freeze = false
  Group = -> [Constraints,Elements,Parts]
  Verbose = false
  _LinkVersion = 1
  _SolverType = 1
  _Version = 1
FEATURE [App::FeaturePython] Constraints  # WARN: FeaturePython — macro-defined, semantics opaque (R4)
  Group = -> [Constraint006,Constraint007,Constraint,Constraint008,Constraint009,Constraint010,Constraint011,Constraint012]
  _LinkVersion = 1
  _Version = 1
FEATURE [App::FeaturePython] Elements  # WARN: FeaturePython — macro-defined, semantics opaque (R4)
  Group = -> [_Element012,_Element013,_Element014,Element,Element001,Element002,Element003,_Element,_Element015,_Element016,_Element017,_Element018,_Element019,_Element020,_Element021,_Element022,_Element023,_Element024,_Element025]
  _LinkVersion = 1
FEATURE [App::FeaturePython] Constraint006  label="Attachment006"  # WARN: FeaturePython — macro-defined, semantics opaque (R4)
  Cascade = false
  Disabled = false
  Group = -> [ElementLink012,ElementLink013]
  Multiply = false
  _ConstraintType = 45
  _LinkVersion = 1
  _Parent = -> Constraints
FEATURE [App::FeaturePython] ElementLink012  label="_Element012"  # link proxy (typed FeaturePython)
  LinkTransform = true
  LinkedObject = -> _Element012
  _LinkVersion = 1
  _Parent = -> Constraint006
FEATURE [Part::FeaturePython] _Element012  # link proxy (typed FeaturePython)
  Detach = false
  LinkTransform = true
  LinkedObject = -> Link001 [Chamfer.Edge58]
  _LinkVersion = 1
  _Parent = -> Elements
FEATURE [App::FeaturePython] ElementLink013  label="Nut-mate"  # link proxy (typed FeaturePython)
  LinkTransform = true
  LinkedObject = -> _Element013
  _LinkVersion = 1
  _Parent = -> Constraint006
FEATURE [Part::FeaturePython] _Element013  label="Nut-mate"  # link proxy (typed FeaturePython)
  Detach = false
  LinkTransform = true
  LinkedObject = -> Link [Chamfer001.Edge6]
  _LinkVersion = 1
  _Parent = -> Elements
FEATURE [App::FeaturePython] Constraint007  label="Locked"  # WARN: FeaturePython — macro-defined, semantics opaque (R4)
  Disabled = false
  Group = -> [ElementLink014]
  _ConstraintType = 0
  _LinkVersion = 1
  _Parent = -> Constraints
FEATURE [App::FeaturePython] ElementLink014  label="_Element014"  # link proxy (typed FeaturePython)
  LinkTransform = true
  LinkedObject = -> _Element014
  _LinkVersion = 1
  _Parent = -> Constraint007
FEATURE [Part::FeaturePython] _Element014  # link proxy (typed FeaturePython)
  Detach = false
  LinkTransform = true
  LinkedObject = -> Link001 [Chamfer.Face1]
  _LinkVersion = 1
  _Parent = -> Elements
FEATURE [Part::FeaturePython] Element  label="gov-mate"  # link proxy (typed FeaturePython)
  Detach = false
  LinkTransform = true
  LinkedObject = -> Link001 [Chamfer.Edge7]
  _LinkVersion = 1
  _Parent = -> Elements
FEATURE [Part::FeaturePython] Element001  label="Axis"  # link proxy (typed FeaturePython)
  Detach = false
  LinkTransform = true
  LinkedObject = -> Link001 [DatumLine.]
  _LinkVersion = 1
  _Parent = -> Elements
FEATURE [Part::FeaturePython] Element002  label="gov-mate-r"  # link proxy (typed FeaturePython)
  Detach = false
  LinkTransform = true
  LinkedObject = -> Link001 [Chamfer.Edge5]
  _LinkVersion = 1
  _Parent = -> Elements
FEATURE [Part::FeaturePython] Element003  label="shim-mate"  # link proxy (typed FeaturePython)
  Detach = false
  LinkTransform = true
  LinkedObject = -> Link001 [Chamfer.Edge8]
  _LinkVersion = 1
  _Parent = -> Elements
FEATURE [App::FeaturePython] Constraint  label="Attachment"  # WARN: FeaturePython — macro-defined, semantics opaque (R4)
  Cascade = false
  Disabled = false
  Group = -> [ElementLink,ElementLink015]
  Multiply = false
  _ConstraintType = 45
  _LinkVersion = 0
  _Parent = -> Constraints
FEATURE [App::FeaturePython] ElementLink  label="_Element"  # link proxy (typed FeaturePython)
  LinkTransform = true
  LinkedObject = -> _Element
  _LinkVersion = 0
  _Parent = -> Constraint
FEATURE [Part::FeaturePython] _Element  # link proxy (typed FeaturePython)
  Detach = false
  LinkTransform = true
  LinkedObject = -> Link002 [0.Edge4]
  _LinkVersion = 0
  _Parent = -> Elements
FEATURE [App::FeaturePython] ElementLink015  label="_Element015"  # link proxy (typed FeaturePython)
  LinkTransform = true
  LinkedObject = -> _Element015
  _LinkVersion = 0
  _Parent = -> Constraint
FEATURE [Part::FeaturePython] _Element015  # link proxy (typed FeaturePython)
  Detach = false
  LinkTransform = true
  LinkedObject = -> Link [Chamfer001.Edge40]
  _LinkVersion = 0
  _Parent = -> Elements
FEATURE [App::FeaturePython] Constraint008  label="Attachment007"  # WARN: FeaturePython — macro-defined, semantics opaque (R4)
  Cascade = false
  Disabled = false
  Group = -> [ElementLink016,ElementLink017]
  Multiply = false
  _ConstraintType = 45
  _LinkVersion = 0
  _Parent = -> Constraints
FEATURE [App::FeaturePython] ElementLink016  label="_Element016"  # link proxy (typed FeaturePython)
  LinkTransform = true
  LinkedObject = -> _Element016
  _LinkVersion = 0
  _Parent = -> Constraint008
FEATURE [Part::FeaturePython] _Element016  # link proxy (typed FeaturePython)
  Detach = false
  LinkTransform = true
  LinkedObject = -> Link002 [1.Edge4]
  _LinkVersion = 0
  _Parent = -> Elements
FEATURE [App::FeaturePython] ElementLink017  label="_Element017"  # link proxy (typed FeaturePython)
  LinkTransform = true
  LinkedObject = -> _Element017
  _LinkVersion = 0
  _Parent = -> Constraint008
FEATURE [Part::FeaturePython] _Element017  # link proxy (typed FeaturePython)
  Detach = false
  LinkTransform = true
  LinkedObject = -> Link [Chamfer001.Edge39]
  _LinkVersion = 0
  _Parent = -> Elements
FEATURE [App::FeaturePython] Constraint009  label="Attachment008"  # WARN: FeaturePython — macro-defined, semantics opaque (R4)
  Cascade = false
  Disabled = false
  Group = -> [ElementLink018,ElementLink019]
  Multiply = false
  _ConstraintType = 45
  _LinkVersion = 0
  _Parent = -> Constraints
FEATURE [App::FeaturePython] ElementLink018  label="_Element018"  # link proxy (typed FeaturePython)
  LinkTransform = true
  LinkedObject = -> _Element018
  _LinkVersion = 0
  _Parent = -> Constraint009
FEATURE [Part::FeaturePython] _Element018  # link proxy (typed FeaturePython)
  Detach = false
  LinkTransform = true
  LinkedObject = -> Link002 [2.Edge4]
  _LinkVersion = 0
  _Parent = -> Elements
FEATURE [App::FeaturePython] ElementLink019  label="_Element019"  # link proxy (typed FeaturePython)
  LinkTransform = true
  LinkedObject = -> _Element019
  _LinkVersion = 0
  _Parent = -> Constraint009
FEATURE [Part::FeaturePython] _Element019  # link proxy (typed FeaturePython)
  Detach = false
  LinkTransform = true
  LinkedObject = -> Link [Chamfer001.Edge38]
  _LinkVersion = 0
  _Parent = -> Elements
FEATURE [App::FeaturePython] Constraint010  label="Attachment009"  # WARN: FeaturePython — macro-defined, semantics opaque (R4)
  Cascade = false
  Disabled = false
  Group = -> [ElementLink020,ElementLink021]
  Multiply = false
  _ConstraintType = 45
  _LinkVersion = 0
  _Parent = -> Constraints
FEATURE [App::FeaturePython] ElementLink020  label="_Element020"  # link proxy (typed FeaturePython)
  LinkTransform = true
  LinkedObject = -> _Element020
  _LinkVersion = 0
  _Parent = -> Constraint010
FEATURE [Part::FeaturePython] _Element020  # link proxy (typed FeaturePython)
  Detach = false
  LinkTransform = true
  LinkedObject = -> Link002 [3.Edge4]
  _LinkVersion = 0
  _Parent = -> Elements
FEATURE [App::FeaturePython] ElementLink021  label="_Element021"  # link proxy (typed FeaturePython)
  LinkTransform = true
  LinkedObject = -> _Element021
  _LinkVersion = 0
  _Parent = -> Constraint010
FEATURE [Part::FeaturePython] _Element021  # link proxy (typed FeaturePython)
  Detach = false
  LinkTransform = true
  LinkedObject = -> Link [Chamfer001.Edge43]
  _LinkVersion = 0
  _Parent = -> Elements
FEATURE [App::FeaturePython] Constraint011  label="Attachment010"  # WARN: FeaturePython — macro-defined, semantics opaque (R4)
  Cascade = false
  Disabled = false
  Group = -> [ElementLink022,ElementLink023]
  Multiply = false
  _ConstraintType = 45
  _LinkVersion = 0
  _Parent = -> Constraints
FEATURE [App::FeaturePython] ElementLink022  label="_Element022"  # link proxy (typed FeaturePython)
  LinkTransform = true
  LinkedObject = -> _Element022
  _LinkVersion = 0
  _Parent = -> Constraint011
FEATURE [Part::FeaturePython] _Element022  # link proxy (typed FeaturePython)
  Detach = false
  LinkTransform = true
  LinkedObject = -> Link002 [4.Edge4]
  _LinkVersion = 0
  _Parent = -> Elements
FEATURE [App::FeaturePython] ElementLink023  label="_Element023"  # link proxy (typed FeaturePython)
  LinkTransform = true
  LinkedObject = -> _Element023
  _LinkVersion = 0
  _Parent = -> Constraint011
FEATURE [Part::FeaturePython] _Element023  # link proxy (typed FeaturePython)
  Detach = false
  LinkTransform = true
  LinkedObject = -> Link [Chamfer001.Edge41]
  _LinkVersion = 0
  _Parent = -> Elements
FEATURE [App::FeaturePython] Constraint012  label="Attachment011"  # WARN: FeaturePython — macro-defined, semantics opaque (R4)
  Cascade = false
  Disabled = false
  Group = -> [ElementLink024,ElementLink025]
  Multiply = false
  _ConstraintType = 45
  _LinkVersion = 0
  _Parent = -> Constraints
FEATURE [App::FeaturePython] ElementLink024  label="_Element024"  # link proxy (typed FeaturePython)
  LinkTransform = true
  LinkedObject = -> _Element024
  _LinkVersion = 0
  _Parent = -> Constraint012
FEATURE [Part::FeaturePython] _Element024  # link proxy (typed FeaturePython)
  Detach = false
  LinkTransform = true
  LinkedObject = -> Link002 [5.Edge4]
  _LinkVersion = 0
  _Parent = -> Elements
FEATURE [App::FeaturePython] ElementLink025  label="_Element025"  # link proxy (typed FeaturePython)
  LinkTransform = true
  LinkedObject = -> _Element025
  _LinkVersion = 0
  _Parent = -> Constraint012
FEATURE [Part::FeaturePython] _Element025  # link proxy (typed FeaturePython)
  Detach = false
  LinkTransform = true
  LinkedObject = -> Link [Chamfer001.Edge42]
  _LinkVersion = 0
  _Parent = -> Elements
---- part parts/HGH20CA.FCStd = doc fcstd_d22bc38b7fa2 ----
FCSTD DOCUMENT  (FreeCAD 2021.614R24301 +3747 (Git))
Label: HGH20CA
License: Creative Commons Attribution
LicenseURL: http://creativecommons.org/licenses/by/4.0/
objects: Part::FeaturePython×21, App::FeaturePython×20, Sketcher::SketchObject×11, PartDesign::Pad×6, PartDesign::Pocket×4, App::Link×4, PartDesign::Plane×2, PartDesign::Body×2, App::DocumentObjectGroup×2, PartDesign::Mirrored×1, PartDesign::Fillet×1, PartDesign::Line×1, PartDesign::Revolution×1
note: 74 computed .brp shape members not serialized (recipe doc carries the construction recipe); baked Part::Feature solids carry a one-line shape summary decoded from their .brp

FEATURE [Sketcher::SketchObject] Sketch
  FullyConstrained = true
  MapMode = 5
  Placement = pos=(0,0,0) rot=(1,0,0;1.5708rad)
  Support = -> [XZ_Plane]
  sketch-geometry (20):
    g0: LineSegment StartX=-21 StartY=30 StartZ=0 EndX=-11.5 EndY=30 EndZ=0
    g1: LineSegment StartX=22 StartY=29 StartZ=0 EndX=22 EndY=6.1 EndZ=0
    g2: LineSegment StartX=20.5 StartY=4.6 StartZ=0 EndX=-20.5 EndY=4.6 EndZ=0
    g3: LineSegment StartX=-21.6 StartY=5.7 StartZ=0 EndX=-21.6 EndY=22 EndZ=0
    g4: GeomPoint [constr] X=0 Y=4.6 Z=0
    g5: LineSegment StartX=-20.5 StartY=4.6 StartZ=0 EndX=-21.6 EndY=5.7 EndZ=0
    g6: LineSegment StartX=20.5 StartY=4.6 StartZ=0 EndX=22 EndY=6.1 EndZ=0
    g7: LineSegment StartX=-22 StartY=29 StartZ=0 EndX=-21 EndY=30 EndZ=0
    g8: LineSegment StartX=21 StartY=30 StartZ=0 EndX=22 EndY=29 EndZ=0
    g9: LineSegment StartX=-11.5 StartY=30 StartZ=0 EndX=-11.5 EndY=29.6 EndZ=0
    g10: LineSegment StartX=-11.5 StartY=29.6 StartZ=0 EndX=-4.25 EndY=29.6 EndZ=0
    g11: LineSegment StartX=-4.25 StartY=29.6 StartZ=0 EndX=-4.25 EndY=30 EndZ=0
    g12: LineSegment StartX=4.25 StartY=30 StartZ=0 EndX=4.25 EndY=29.6 EndZ=0
    g13: LineSegment StartX=4.25 StartY=29.6 StartZ=0 EndX=11.5 EndY=29.6 EndZ=0
    g14: LineSegment StartX=11.5 StartY=29.6 StartZ=0 EndX=11.5 EndY=30 EndZ=0
    g15: LineSegment StartX=11.5 StartY=30 StartZ=0 EndX=21 EndY=30 EndZ=0
    g16: LineSegment StartX=-4.25 StartY=30 StartZ=0 EndX=4.25 EndY=30 EndZ=0
    g17: GeomPoint [constr] X=0 Y=30 Z=0
    g18: LineSegment StartX=-21.6 StartY=22 StartZ=0 EndX=-22 EndY=22 EndZ=0
    g19: LineSegment StartX=-22 StartY=22 StartZ=0 EndX=-22 EndY=29 EndZ=0
  constraints (54):
    c: Horizontal(g0)
    c: Horizontal(g2)
    c: Vertical(g1)
    c: Vertical(g3)
    c: PointOnObject(g4,g-2)
    c: Vertical(g9)
    c: Coincident(g10,g9)
    c: Horizontal(g10)
    c: Coincident(g11,g10)
    c: Vertical(g11)
    c: Vertical(g12)
    c: Coincident(g13,g12)
    c: Horizontal(g13)
    c: Coincident(g14,g13)
    c: Vertical(g14)
    c: Coincident(g0,g7)
    c: Coincident(g15,g8)
    c: Coincident(g1,g8)
    c: Coincident(g16,g12)
    c: Coincident(g15,g14)
    c: Tangent(g0,g15)
    c: Coincident(g0,g9)
    c: Coincident(g16,g11)
    c: Tangent(g0,g16)
    c: Coincident(g1,g6)
    c: Coincident(g2,g6)
    c: Coincident(g2,g5)
    c: Coincident(g3,g5)
    c: Symmetric(g2,g2,g4)
    c: PointOnObject(g17,g-2)
    c: Symmetric(g12,g11,g17)
    c: Equal(g13,g10)
    c: Symmetric(g8,g0,g17)
    c: Horizontal(g12,g10)
    c: DistanceX(g16,g16) = 8.5
    c: DistanceX(g2,g2) = 41
    c: DistanceY(g14,g14) = 0.4
    c: DistanceX(g14,g1) = 10.5
    c: DistanceY(g1,g8) = 1
    c: DistanceY(g-1,g2) = 4.6
    c: DistanceY(g-1,g8) = 30
    c: DistanceY(g2,g1) = 1.5
    c: Horizontal(g18)
    c: Coincident(g19,g18)
    c: Vertical(g19)
    c: DistanceX(g8,g1) = 1
    c: Coincident(g3,g18)
    c: Coincident(g7,g19)
    c: Horizontal(g1,g7)
    c: DistanceX(g7,g1) = 44
    c: DistanceX(g7,g0) = 10.5
    c: DistanceY(g18,g0) = 8
    c: DistanceX(g18,g3) = 0.4
    c: Angle(g2,g5) = 2.35619
FEATURE [PartDesign::Pad] Pad
  ClaimChildren = false
  Direction = (1,1,1)
  Fit = 0
  FitJoin = 0
  InnerFit = 0
  InnerFitJoin = 0
  InnerTaperAngle = 0
  InnerTaperAngleRev = 0
  Length = 50.5
  Length2 = 100
  Linearize = true
  Midplane = true
  NewSolid = false
  Placement = pos=(0,0,0) rot=(1,0,0;1.5708rad)
  Profile = -> Sketch
  Refine = true
  Suppress = false
  Type = 0
FEATURE [Sketcher::SketchObject] Sketch001
  ExternalGeometry = -> [Pad]
  FullyConstrained = true
  MapMode = 5
  Placement = pos=(0,1.32e-14,30) rot=(0,0,1;3.14159rad)
  Support = -> [Pad]
  sketch-geometry (4):
    g0: Circle CenterX=-16 CenterY=18 CenterZ=0 NormalX=0 NormalY=0 NormalZ=1 AngleXU=0 Radius=2.5
    g1: Circle CenterX=-16 CenterY=-18 CenterZ=0 NormalX=0 NormalY=0 NormalZ=1 AngleXU=0 Radius=2.5
    g2: Circle CenterX=16 CenterY=18 CenterZ=0 NormalX=0 NormalY=0 NormalZ=1 AngleXU=0 Radius=2.5
    g3: Circle CenterX=16 CenterY=-18 CenterZ=0 NormalX=0 NormalY=0 NormalZ=1 AngleXU=0 Radius=2.5
  constraints (12):
    c: Horizontal(g3,g1)
    c: Vertical(g1,g0)
    c: Vertical(g2,g3)
    c: Horizontal(g0,g2)
    c: DistanceX(g0,g2) = 32
    c: DistanceY(g3,g2) = 36
    c: Equal(g0,g2)
    c: Equal(g2,g3)
    c: Equal(g3,g1)
    c: Symmetric(g0,g3,g-1)
    c: DistanceX(g2,g-3) = 5.6
    c: Diameter(g2) = 5
FEATURE [Sketcher::SketchObject] Sketch002
  ExternalGeometry = -> [Pad]
  FullyConstrained = true
  MapMode = 5
  Placement = pos=(0,0,0) rot=(1,0,0;1.5708rad)
  Support = -> [XZ_Plane]
  sketch-geometry (8):
    g0: LineSegment StartX=-20.6 StartY=29.1 StartZ=0 EndX=20.4 EndY=29.1 EndZ=0
    g1: LineSegment StartX=21.4 StartY=28.1 StartZ=0 EndX=21.4 EndY=5.5 EndZ=0
    g2: LineSegment StartX=20.5 StartY=4.6 StartZ=0 EndX=-20.5 EndY=4.6 EndZ=0
    g3: LineSegment StartX=-21.6 StartY=5.7 StartZ=0 EndX=-21.6 EndY=28.1 EndZ=0
    g4: LineSegment StartX=-21.6 StartY=5.7 StartZ=0 EndX=-20.5 EndY=4.6 EndZ=0
    g5: LineSegment StartX=-21.6 StartY=28.1 StartZ=0 EndX=-20.6 EndY=29.1 EndZ=0
    g6: LineSegment StartX=20.4 StartY=29.1 StartZ=0 EndX=21.4 EndY=28.1 EndZ=0
    g7: LineSegment StartX=20.5 StartY=4.6 StartZ=0 EndX=21.4 EndY=5.5 EndZ=0
  constraints (22):
    c: Horizontal(g0)
    c: Horizontal(g2)
    c: Vertical(g1)
    c: Vertical(g3)
    c: Coincident(g3,g4)
    c: Coincident(g2,g4)
    c: Coincident(g2,g-7)
    c: Coincident(g3,g-7)
    c: Coincident(g0,g5)
    c: Coincident(g3,g5)
    c: Coincident(g0,g6)
    c: Coincident(g1,g6)
    c: Horizontal(g1,g3)
    c: DistanceX(g3,g0) = 1
    c: DistanceY(g3,g0) = 1
    c: DistanceX(g0,g1) = 1
    c: DistanceY(g2,g0) = 24.5
    c: DistanceX(g3,g1) = 43
    c: Coincident(g7,g-5)
    c: PointOnObject(g7,g-5)
    c: Coincident(g1,g7)
    c: PointOnObject(g2,g7)
FEATURE [PartDesign::Pad] Pad001
  BaseFeature = -> Pad
  ClaimChildren = false
  Direction = (1,1,1)
  Fit = 0
  FitJoin = 0
  InnerFit = 0
  InnerFitJoin = 0
  InnerTaperAngle = 0
  InnerTaperAngleRev = 0
  Length = 75.8
  Length2 = 100
  Linearize = true
  Midplane = true
  NewSolid = false
  Placement = pos=(0,0,0) rot=(1,0,0;1.5708rad)
  Profile = -> Sketch002
  Refine = true
  Suppress = false
  Type = 0
FEATURE [Sketcher::SketchObject] Sketch003
  ExternalGeometry = -> [Pad001]
  FullyConstrained = true
  MapMode = 5
  Placement = pos=(0,-37.9,8.3e-15) rot=(1,0,0;1.5708rad)
  Support = -> [Pad001]
  sketch-geometry (14):
    g0: ArcOfCircle CenterX=0 CenterY=24.1 CenterZ=0 NormalX=0 NormalY=0 NormalZ=1 AngleXU=0 Radius=5.25 StartAngle=3.14159 EndAngle=6.28319
    g1: ArcOfCircle CenterX=-19.35 CenterY=15.6 CenterZ=0 NormalX=0 NormalY=0 NormalZ=1 AngleXU=0 Radius=2.75 StartAngle=4.71239 EndAngle=7.85398
    g2: ArcOfCircle CenterX=19.35 CenterY=15.6 CenterZ=0 NormalX=0 NormalY=0 NormalZ=1 AngleXU=0 Radius=2.75 StartAngle=1.5708 EndAngle=4.71239
    g3: LineSegment StartX=-5.25 StartY=24.1 StartZ=0 EndX=-5.25 EndY=29.1 EndZ=0
    g4: LineSegment StartX=5.25 StartY=24.1 StartZ=0 EndX=5.25 EndY=29.1 EndZ=0
    g5: LineSegment StartX=-5.25 StartY=29.1 StartZ=0 EndX=5.25 EndY=29.1 EndZ=0
    g6: LineSegment StartX=-19.35 StartY=18.35 StartZ=0 EndX=-21.6 EndY=18.35 EndZ=0
    g7: LineSegment StartX=-19.35 StartY=12.85 StartZ=0 EndX=-21.6 EndY=12.85 EndZ=0
    g8: LineSegment [constr] StartX=-19.35 StartY=15.6 StartZ=0 EndX=0 EndY=15.6 EndZ=0
    g9: LineSegment [constr] StartX=0 StartY=15.6 StartZ=0 EndX=19.35 EndY=15.6 EndZ=0
    g10: LineSegment StartX=19.35 StartY=18.35 StartZ=0 EndX=21.4 EndY=18.35 EndZ=0
    g11: LineSegment StartX=19.35 StartY=12.85 StartZ=0 EndX=21.4 EndY=12.85 EndZ=0
    g12: LineSegment StartX=-21.6 StartY=18.35 StartZ=0 EndX=-21.6 EndY=12.85 EndZ=0
    g13: LineSegment StartX=21.4 StartY=18.35 StartZ=0 EndX=21.4 EndY=12.85 EndZ=0
  constraints (38):
    c: PointOnObject(g0,g-2)
    c: Horizontal(g1,g2)
    c: Equal(g1,g2)
    c: Diameter(g0) = 10.5
    c: DistanceY(g0,g-3) = 5
    c: PointOnObject(g3,g-3)
    c: Vertical(g3)
    c: PointOnObject(g4,g-3)
    c: Vertical(g4)
    c: Tangent(g0,g3) = 1.5708
    c: Tangent(g0,g4) = -1.5708
    c: Coincident(g5,g3)
    c: Coincident(g5,g4)
    c: PointOnObject(g6,g-4)
    c: Horizontal(g6)
    c: PointOnObject(g7,g-4)
    c: Horizontal(g7)
    c: Diameter(g1) = 5.5
    c: Coincident(g8,g1)
    c: Horizontal(g8)
    c: Coincident(g9,g8)
    c: Coincident(g9,g2)
    c: Equal(g9,g8)
    c: PointOnObject(g10,g-5)
    c: Horizontal(g10)
    c: PointOnObject(g11,g-5)
    c: Horizontal(g11)
    c: DistanceY(g2,g-3) = 13.5
    c: DistanceX(g-4,g1) = 2.25
    c: PointOnObject(g8,g-2)
    c: Tangent(g1,g7) = 1.5708
    c: Tangent(g1,g6) = -1.5708
    c: Tangent(g2,g10) = 1.5708
    c: Tangent(g2,g11) = -1.5708
    c: Coincident(g12,g6)
    c: Coincident(g12,g7)
    c: Coincident(g13,g10)
    c: Coincident(g13,g11)
FEATURE [PartDesign::Pocket] Pocket
  BaseFeature = -> Pad001
  ClaimChildren = false
  Fit = 0
  FitJoin = 0
  InnerFit = 0
  InnerFitJoin = 0
  InnerTaperAngle = 0
  InnerTaperAngleRev = 0
  Length = 1.5
  Length2 = 100
  Linearize = true
  NewSolid = false
  Placement = pos=(0,0,0) rot=(1,0,0;1.5708rad)
  Profile = -> Sketch003
  Refine = true
  Suppress = false
  Type = 0
FEATURE [Sketcher::SketchObject] Sketch004
  ExternalGeometry = -> [Pocket]
  FullyConstrained = true
  MapMode = 5
  Placement = pos=(0,-36.4,2.95e-14) rot=(1,0,0;1.5708rad)
  Support = -> [Pocket]
  sketch-geometry (3):
    g0: Circle CenterX=-19.35 CenterY=15.6 CenterZ=0 NormalX=0 NormalY=0 NormalZ=1 AngleXU=0 Radius=1.25
    g1: Circle CenterX=19.35 CenterY=15.6 CenterZ=0 NormalX=0 NormalY=0 NormalZ=1 AngleXU=0 Radius=1.25
    g2: Circle CenterX=0 CenterY=24.1 CenterZ=0 NormalX=0 NormalY=0 NormalZ=1 AngleXU=0 Radius=2.5
  constraints (6):
    c: Coincident(g0,g-3)
    c: Coincident(g1,g-5)
    c: Coincident(g2,g-4)
    c: Diameter(g2) = 5
    c: Diameter(g1) = 2.5
    c: Equal(g1,g0)
FEATURE [PartDesign::Pocket] Pocket001
  BaseFeature = -> Pocket
  ClaimChildren = false
  Fit = 0
  FitJoin = 0
  InnerFit = 0
  InnerFitJoin = 0
  InnerTaperAngle = 0
  InnerTaperAngleRev = 0
  Length = 8
  Length2 = 100
  Linearize = true
  NewSolid = false
  Placement = pos=(0,0,0) rot=(1,0,0;1.5708rad)
  Profile = -> Sketch004
  Refine = true
  Suppress = false
  Type = 0
FEATURE [PartDesign::Mirrored] Mirrored
  BaseFeature = -> Pocket001
  CopyShape = false
  MirrorPlane = -> XZ_Plane
  NewSolid = false
  OriginalSubs = -> [Pocket001,Pocket]
  Originals = -> [Pocket001,Pocket]
  ParallelTransform = true
  Placement = pos=(0,0,0) rot=(1,0,0;1.5708rad)
  Refine = true
  SubTransform = true
  Suppress = false
  _Version = 1
FEATURE [Sketcher::SketchObject] Sketch005
  FullyConstrained = true
  MapMode = 5
  Placement = pos=(0,0,0) rot=(1,0,0;1.5708rad)
  Support = -> [XZ_Plane001]
  sketch-geometry (1):
    g0: Circle CenterX=0 CenterY=0 CenterZ=0 NormalX=0 NormalY=0 NormalZ=1 AngleXU=0 Radius=3
  constraints (2):
    c: Coincident(g0,g-1)
    c: Radius(g0) = 3
FEATURE [PartDesign::Pad] Pad002
  ClaimChildren = false
  Direction = (1,1,1)
  Fit = 0
  FitJoin = 0
  InnerFit = 0
  InnerFitJoin = 0
  InnerTaperAngle = 0
  InnerTaperAngleRev = 0
  Length = 7
  Length2 = 100
  Linearize = true
  NewSolid = false
  Placement = pos=(0,0,0) rot=(1,0,0;1.5708rad)
  Profile = -> Sketch005
  Refine = true
  Suppress = false
  Type = 0
FEATURE [Sketcher::SketchObject] Sketch006
  FullyConstrained = true
  MapMode = 5
  Placement = pos=(0,0,0) rot=(-1,0,0;1.5708rad)
  Support = -> [Pad002]
  sketch-geometry (7):
    g0: LineSegment StartX=4 StartY=-2.3094 StartZ=0 EndX=4 EndY=2.3094 EndZ=0
    g1: LineSegment StartX=4 StartY=2.3094 StartZ=0 EndX=-4e-16 EndY=4.6188 EndZ=0
    g2: LineSegment StartX=-4e-16 StartY=4.6188 StartZ=0 EndX=-4 EndY=2.3094 EndZ=0
    g3: LineSegment StartX=-4 StartY=2.3094 StartZ=0 EndX=-4 EndY=-2.3094 EndZ=0
    g4: LineSegment StartX=-4 StartY=-2.3094 StartZ=0 EndX=4e-16 EndY=-4.6188 EndZ=0
    g5: LineSegment StartX=4e-16 StartY=-4.6188 StartZ=0 EndX=4 EndY=-2.3094 EndZ=0
    g6: Circle [constr] CenterX=0 CenterY=0 CenterZ=0 NormalX=0 NormalY=0 NormalZ=1 AngleXU=0 Radius=4.6188
  constraints (16):
    c: Coincident(g0,g1)
    c: Coincident(g1,g2)
    c: Coincident(g2,g3)
    c: Coincident(g3,g4)
    c: Coincident(g4,g5)
    c: Coincident(g5,g0)
    c: Equal(g0, g1-g5) x5
    c: PointOnObject(g0,g6)
    c: PointOnObject(g1,g6)
    c: PointOnObject(g2,g6)
    c: PointOnObject(g3,g6)
    c: PointOnObject(g4,g6)
    c: PointOnObject(g5,g6)
    c: Coincident(g6,g-1)
    c: Vertical(g0)
    c: DistanceX(g2,g0) = 8
FEATURE [PartDesign::Pad] Pad003
  BaseFeature = -> Pad002
  ClaimChildren = false
  Direction = (1,1,1)
  Fit = 0
  FitJoin = 0
  InnerFit = 0
  InnerFitJoin = 0
  InnerTaperAngle = 0
  InnerTaperAngleRev = 0
  Length = 3.5
  Length2 = 100
  Linearize = true
  NewSolid = false
  Placement = pos=(0,0,0) rot=(1,0,0;1.5708rad)
  Profile = -> Sketch006
  Refine = true
  Suppress = false
  Type = 0
FEATURE [Sketcher::SketchObject] Sketch007
  FullyConstrained = true
  MapMode = 5
  Placement = pos=(0,3.5,8e-16) rot=(-1,0,0;1.5708rad)
  Support = -> [Pad003]
  sketch-geometry (1):
    g0: Circle CenterX=0 CenterY=0 CenterZ=0 NormalX=0 NormalY=0 NormalZ=1 AngleXU=0 Radius=4
  constraints (2):
    c: Coincident(g0,g-1)
    c: Radius(g0) = 4
FEATURE [PartDesign::Pad] Pad004
  BaseFeature = -> Pad003
  ClaimChildren = false
  Direction = (1,1,1)
  Fit = 0
  FitJoin = 0
  InnerFit = 0
  InnerFitJoin = 0
  InnerTaperAngle = 0
  InnerTaperAngleRev = 0
  Length = 8
  Length2 = 100
  Linearize = true
  NewSolid = false
  Placement = pos=(0,0,0) rot=(1,0,0;1.5708rad)
  Profile = -> Sketch007
  Refine = true
  Suppress = false
  Type = 0
FEATURE [PartDesign::Fillet] Fillet
  Base = -> Pad004 [Edge35]
  BaseFeature = -> Pad004
  NewSolid = false
  Placement = pos=(0,0,0) rot=(1,0,0;1.5708rad)
  Radius = 3
  Refine = true
  SupportTransform = false
  Suppress = false
FEATURE [PartDesign::Plane] DatumPlane
  AttachmentOffset = pos=(0,0,0) rot=(1,0,0;0.785398rad)
  Length = 50
  MapMode = 5
  MinimumLength = 10
  MinimumWidth = 10
  Placement = pos=(0,11.5,3e-15) rot=(-1,0,0;0.785398rad)
  ResizeMode = 0
  Support = -> [Fillet]
  Width = 70.7107
FEATURE [Sketcher::SketchObject] Sketch008
  FullyConstrained = true
  MapMode = 5
  Placement = pos=(0,11.5,3.6e-15) rot=(-1,0,0;0.785398rad)
  Support = -> [DatumPlane]
  sketch-geometry (7):
    g0: LineSegment StartX=3.5 StartY=-4.62073 StartZ=0 EndX=3.5 EndY=-0.579274 EndZ=0
    g1: LineSegment StartX=3.5 StartY=-0.579274 StartZ=0 EndX=8.273e-13 EndY=1.44145 EndZ=0
    g2: LineSegment StartX=8.273e-13 StartY=1.44145 StartZ=0 EndX=-3.5 EndY=-0.579274 EndZ=0
    g3: LineSegment StartX=-3.5 StartY=-0.579274 StartZ=0 EndX=-3.5 EndY=-4.62073 EndZ=0
    g4: LineSegment StartX=-3.5 StartY=-4.62073 StartZ=0 EndX=-8.273e-13 EndY=-6.64145 EndZ=0
    g5: LineSegment StartX=-8.273e-13 StartY=-6.64145 StartZ=0 EndX=3.5 EndY=-4.62073 EndZ=0
    g6: Circle [constr] CenterX=0 CenterY=-2.6 CenterZ=0 NormalX=0 NormalY=0 NormalZ=1 AngleXU=0 Radius=4.04145
  constraints (17):
    c: Coincident(g0,g1)
    c: Coincident(g1,g2)
    c: Coincident(g2,g3)
    c: Coincident(g3,g4)
    c: Coincident(g4,g5)
    c: Coincident(g5,g0)
    c: Equal(g0, g1-g5) x5
    c: PointOnObject(g0,g6)
    c: PointOnObject(g1,g6)
    c: PointOnObject(g2,g6)
    c: PointOnObject(g3,g6)
    c: PointOnObject(g4,g6)
    c: PointOnObject(g5,g6)
    c: PointOnObject(g6,g-2)
    c: Vertical(g0)
    c: DistanceX(g2,g0) = 7
    c: DistanceY(g6,g-1) = 2.6
FEATURE [PartDesign::Pad] Pad005
  BaseFeature = -> Fillet
  ClaimChildren = false
  Direction = (1,1,1)
  Fit = 0
  FitJoin = 0
  InnerFit = 0
  InnerFitJoin = 0
  InnerTaperAngle = 0
  InnerTaperAngleRev = 0
  Length = 2.5
  Length2 = 100
  Linearize = true
  NewSolid = false
  Placement = pos=(0,0,0) rot=(1,0,0;1.5708rad)
  Profile = -> Sketch008
  Refine = true
  Suppress = false
  Type = 0
FEATURE [PartDesign::Plane] DatumPlane001
  AttachmentOffset = pos=(0,0,0) rot=(0,1,0;1.5708rad)
  Length = 70.7107
  MapMode = 5
  MinimumLength = 10
  MinimumWidth = 10
  Placement = pos=(2e-16,7.51777,7.51777) rot=(-0.357407,0.862856,-0.357407;1.71777rad)
  ResizeMode = 0
  Support = -> [Pad005]
  Width = 70.7107
FEATURE [Sketcher::SketchObject] Sketch009
  ExternalGeometry = -> [Pad005]
  FullyConstrained = true
  MapMode = 5
  Placement = pos=(2e-16,7.51777,7.51777) rot=(-0.357407,0.862856,-0.357407;1.71777rad)
  Support = -> [DatumPlane001]
  sketch-geometry (7):
    g0: LineSegment StartX=0 StartY=8.43173 StartZ=0 EndX=-2 EndY=7.78173 EndZ=0
    g1: LineSegment StartX=-4 StartY=8.78173 StartZ=0 EndX=-5.5 EndY=7.78173 EndZ=0
    g2: LineSegment StartX=-5.5 StartY=7.78173 StartZ=0 EndX=-5.5 EndY=5.53173 EndZ=0
    g3: LineSegment StartX=-5.5 StartY=5.53173 StartZ=0 EndX=1.8e-15 EndY=5.53173 EndZ=0
    g4: LineSegment StartX=1.8e-15 StartY=5.53173 StartZ=0 EndX=0 EndY=8.43173 EndZ=0
    g5: LineSegment StartX=-4 StartY=8.78173 StartZ=0 EndX=-3.5 EndY=8.78173 EndZ=0
    g6: LineSegment StartX=-3.5 StartY=8.78173 StartZ=0 EndX=-2 EndY=7.78173 EndZ=0
  constraints (20):
    c: PointOnObject(g0,g-2)
    c: Vertical(g2)
    c: Coincident(g3,g2)
    c: Horizontal(g3)
    c: Coincident(g4,g3)
    c: Coincident(g4,g0)
    c: Symmetric(g-3,g-4,g3)
    c: DistanceY(g4,g4) = 2.9
    c: DistanceX(g3,g3) = 5.5
    c: Coincident(g2,g1)
    c: DistanceX(g1,g1) = 1.5
    c: Coincident(g5,g1)
    c: Coincident(g6,g5)
    c: Coincident(g6,g0)
    c: Horizontal(g5)
    c: DistanceX(g5,g0) = 1.5
    c: Horizontal(g1,g0)
    c: DistanceX(g1,g0) = 3.5
    c: DistanceY(g2,g2) = 2.25
    c: DistanceY(g2,g1) = 3.25
FEATURE [PartDesign::Line] DatumLine
  AttacherType = Attacher::AttachEngineLine
  Length = 70.7107
  MapMode = 29
  MinimumLength = 10
  Placement = pos=(2e-16,11.4293,3.60624) rot=(1,0,0;2.35619rad)
  ResizeMode = 0
  Support = -> [Sketch009]
FEATURE [PartDesign::Revolution] Revolution
  Angle = 360
  Axis = (0,-0.707107,-0.707107)
  Base = (2e-16,11.4293,3.60624)
  BaseFeature = -> Pad005
  ClaimChildren = false
  Fit = 0
  FitJoin = 0
  InnerFit = 0
  InnerFitJoin = 0
  NewSolid = false
  Placement = pos=(0,0,0) rot=(1,0,0;1.5708rad)
  Profile = -> Sketch009
  ReferenceAxis = -> DatumLine
  Refine = true
  Suppress = false
FEATURE [PartDesign::Body] Body001  label="Greaser"
  AutoGroupSolids = false
  ExportMode = 0
  Group = -> [Sketch005,Pad002,Sketch006,Pad003,Sketch007,Pad004,Fillet,DatumPlane,Sketch008,Pad005,DatumPlane001,Sketch009,DatumLine,Revolution]
  Origin = -> Origin001
  Placement = pos=(0.291005,-51,25.9599) rot=(-0.793353,0,0.608761;3.14159rad)
  Tip = -> Revolution
  _ExportChildren = -> [Pad002,Pad003,Pad004,Fillet,DatumPlane,Pad005,DatumPlane001,DatumLine,Revolution]
  _GroupVersion = 1
FEATURE [App::Link] Link001  label="Link001(HGH20CA)"
  AutoLinkLabel = true
  LinkedObject = -> Body
  SyncGroupVisibility = false
  _LinkVersion = 1
FEATURE [App::Link] Link002  label="Link002(Greaser)"
  AutoLinkLabel = true
  LinkPlacement = pos=(-9e-16,36.4,24.1) rot=(0,-1,0;4.45059rad)
  LinkedObject = -> Body001
  Placement = pos=(-9e-16,36.4,24.1) rot=(0,-1,0;4.45059rad)
  SyncGroupVisibility = false
  _LinkVersion = 1
FEATURE [Part::FeaturePython] Screw  label="M6x8-Screw"  # Fasteners workbench fastener (typed FeaturePython)
  Placement = pos=(0,-36.4,24.1) rot=(1,0,0;1.5708rad)
  diameter = 4
  invert = false
  length = 13
  lengthCustom = 8
  matchOuter = false
  offset = 0
  thread = false
  type = 39
FEATURE [Part::FeaturePython] Parts  # WARN: FeaturePython — macro-defined, semantics opaque (R4)
  Group = -> [Link001,Link002,Screw]
  GroupMode = 0
  _LinkVersion = 1
FEATURE [App::Link] Link003  label="Link003(Greaser)"
  AutoLinkLabel = true
  LinkPlacement = pos=(-1e-16,-36.4,24.1) rot=(-0.793353,0,-0.608761;3.14159rad)
  LinkedObject = -> Body001
  Placement = pos=(-1e-16,-36.4,24.1) rot=(-0.793353,0,-0.608761;3.14159rad)
  SyncGroupVisibility = false
  _LinkVersion = 1
FEATURE [App::Link] Link004  label="Link004(HGH20CA)"
  AutoLinkLabel = true
  LinkedObject = -> Body
  SyncGroupVisibility = false
  _LinkVersion = 1
FEATURE [Part::FeaturePython] Screw001  label="M6x8-Screw001"  # Fasteners workbench fastener (typed FeaturePython)
  Placement = pos=(0,36.4,24.1) rot=(-1,0,0;1.5708rad)
  diameter = 4
  invert = false
  length = 13
  lengthCustom = 8
  matchOuter = false
  offset = 0
  thread = false
  type = 39
FEATURE [Part::FeaturePython] Parts001  # WARN: FeaturePython — macro-defined, semantics opaque (R4)
  Group = -> [Link003,Link004,Screw001]
  GroupMode = 0
  _LinkVersion = 1
FEATURE [Sketcher::SketchObject] Sketch010
  FullyConstrained = true
  MapMode = 5
  Placement = pos=(0,0,0) rot=(1,0,0;1.5708rad)
  Support = -> [XZ_Plane]
  sketch-geometry (29):
    g0: LineSegment StartX=-9 StartY=0 StartZ=0 EndX=-10 EndY=1 EndZ=0
    g1: LineSegment StartX=-10 StartY=1 StartZ=0 EndX=-10 EndY=4 EndZ=0
    g2: LineSegment StartX=-10 StartY=4 StartZ=0 EndX=-6.6 EndY=7.45 EndZ=0
    g3: LineSegment StartX=-6.6 StartY=7.45 StartZ=0 EndX=-6.6 EndY=9.95 EndZ=0
    g4: LineSegment StartX=-6.6 StartY=9.95 StartZ=0 EndX=-7.65996 EndY=11.05 EndZ=0
    g5: ArcOfCircle CenterX=-9.8 CenterY=10.8 CenterZ=0 NormalX=0 NormalY=0 NormalZ=1 AngleXU=0 Radius=2.15459 StartAngle=0.116293 EndAngle=1.47784
    g6: LineSegment StartX=-9.6 StartY=12.9453 StartZ=0 EndX=-10 EndY=13.3453 EndZ=0
    g7: LineSegment StartX=-10 StartY=13.3453 StartZ=0 EndX=-10 EndY=14.6953 EndZ=0
    g8: LineSegment StartX=-10 StartY=14.6953 StartZ=0 EndX=-9.6 EndY=15.0953 EndZ=0
    g9: ArcOfCircle CenterX=-9.8 CenterY=17.2406 CenterZ=0 NormalX=0 NormalY=0 NormalZ=1 AngleXU=0 Radius=2.15459 StartAngle=4.80535 EndAngle=6.21789
    g10: LineSegment StartX=-7.65 StartY=17.1 StartZ=0 EndX=-7.25 EndY=17.5 EndZ=0
    g11: LineSegment StartX=-7.25 StartY=17.5 StartZ=0 EndX=0 EndY=17.5 EndZ=0
    g12: LineSegment StartX=0 StartY=17.5 StartZ=0 EndX=7.25 EndY=17.5 EndZ=0
    g13: LineSegment StartX=7.25 StartY=17.5 StartZ=0 EndX=7.65 EndY=17.1 EndZ=0
    g14: ArcOfCircle CenterX=9.8 CenterY=17.2406 CenterZ=0 NormalX=0 NormalY=0 NormalZ=1 AngleXU=0 Radius=2.15459 StartAngle=3.20688 EndAngle=4.61943
    g15: LineSegment StartX=9.6 StartY=15.0953 StartZ=0 EndX=10 EndY=14.6953 EndZ=0
    g16: LineSegment StartX=10 StartY=14.6953 StartZ=0 EndX=10 EndY=13.3453 EndZ=0
    g17: LineSegment StartX=10 StartY=13.3453 StartZ=0 EndX=9.6 EndY=12.9453 EndZ=0
    g18: ArcOfCircle CenterX=9.8 CenterY=10.8 CenterZ=0 NormalX=0 NormalY=0 NormalZ=1 AngleXU=0 Radius=2.15459 StartAngle=1.66376 EndAngle=3.0253
    g19: LineSegment StartX=7.65996 StartY=11.05 StartZ=0 EndX=6.6 EndY=9.95 EndZ=0
    g20: LineSegment StartX=6.6 StartY=9.95 StartZ=0 EndX=6.6 EndY=7.45 EndZ=0
    g21: LineSegment StartX=6.6 StartY=7.45 StartZ=0 EndX=10 EndY=4 EndZ=0
    g22: LineSegment StartX=10 StartY=4 StartZ=0 EndX=10 EndY=1 EndZ=0
    g23: LineSegment StartX=10 StartY=1 StartZ=0 EndX=9 EndY=0 EndZ=0
    g24: LineSegment StartX=-4 StartY=0 StartZ=0 EndX=-4 EndY=0.4 EndZ=0
    g25: LineSegment StartX=-4 StartY=0.4 StartZ=0 EndX=4 EndY=0.4 EndZ=0
    g26: LineSegment StartX=4 StartY=0.4 StartZ=0 EndX=4 EndY=0 EndZ=0
    g27: LineSegment StartX=-9 StartY=0 StartZ=0 EndX=-4 EndY=0 EndZ=0
    g28: LineSegment StartX=4 StartY=0 StartZ=0 EndX=9 EndY=0 EndZ=0
  constraints (89):
    c: Coincident(g0,g1)
    c: Vertical(g1)
    c: Coincident(g1,g2)
    c: Coincident(g2,g3)
    c: Vertical(g3)
    c: Coincident(g3,g4)
    c: Coincident(g5,g4)
    c: Coincident(g6,g5)
    c: Coincident(g6,g7)
    c: Vertical(g7)
    c: Coincident(g7,g8)
    c: Coincident(g9,g8)
    c: Coincident(g9,g10)
    c: Coincident(g10,g11)
    c: PointOnObject(g11,g-2)
    c: Horizontal(g11)
    c: Coincident(g11,g12)
    c: Horizontal(g12)
    c: Coincident(g12,g13)
    c: Coincident(g14,g13)
    c: Coincident(g14,g15)
    c: Coincident(g15,g16)
    c: Coincident(g16,g17)
    c: Coincident(g18,g17)
    c: Coincident(g18,g19)
    c: Coincident(g19,g20)
    c: Vertical(g20)
    c: Coincident(g20,g21)
    c: Coincident(g21,g22)
    c: Vertical(g22)
    c: Coincident(g22,g23)
    c: PointOnObject(g23,g-1)
    c: Equal(g0,g23)
    c: Equal(g22,g1)
    c: Equal(g2,g21)
    c: Equal(g20,g3)
    c: Equal(g4,g19)
    c: Equal(g5,g18)
    c: Equal(g18,g14)
    c: Equal(g14,g9)
    c: Equal(g15,g17)
    c: Vertical(g16)
    c: Equal(g16,g7)
    c: Equal(g10,g13)
    c: Equal(g12,g11)
    c: DistanceX(g10,g12) = 14.5
    c: Horizontal(g22,g0)
    c: DistanceX(g0,g22) = 20
    c: Horizontal(g2,g20)
    c: DistanceX(g0,g23) = 18
    c: DistanceY(g23,g22) = 1
    c: DistanceY(g22,g22) = 3
    c: DistanceX(g2,g20) = 13.2
    c: DistanceY(g21,g20) = 3.45
    c: DistanceY(g20,g20) = 2.5
    c: Horizontal(g18,g5)
    c: Horizontal(g18,g4)
    c: Horizontal(g9,g13)
    c: Horizontal(g9,g14)
    c: Vertical(g9,g5)
    c: DistanceX(g9,g13) = 15.3
    c: DistanceY(g13,g12) = 0.4
    c: Vertical(g15,g21)
    c: Vertical(g7,g1)
    c: Equal(g13,g15)
    c: Equal(g17,g6)
    c: Equal(g6,g8)
    c: DistanceY(g19,g18) = 1.1
    c: DistanceY(g23,g18) = 10.8
    c: DistanceX(g5,g17) = 19.2
    c: DistanceY(g23,g12) = 17.5
    c: DistanceY(g17,g16) = 0.4
    c: DistanceY(g15,g14) = 0.4
    c: DistanceY(g7,g7) = 1.35
    c: DistanceX(g-1,g18) = 9.8
    c: Coincident(g24,g25)
    c: Horizontal(g25)
    c: Coincident(g25,g26)
    c: Vertical(g26)
    c: Vertical(g24)
    c: Symmetric(g26,g24,g-1)
    c: Coincident(g27,g0)
    c: Coincident(g27,g24)
    c: Horizontal(g27)
    c: Coincident(g28,g26)
    c: Coincident(g28,g23)
    c: DistanceX(g25,g25) = 8
    c: DistanceY(g26,g26) = 0.4
    c: Symmetric(g23,g0,g-1)
FEATURE [PartDesign::Pocket] Pocket002
  BaseFeature = -> Mirrored
  ClaimChildren = false
  Fit = 0
  FitJoin = 0
  InnerFit = 0
  InnerFitJoin = 0
  InnerTaperAngle = 0
  InnerTaperAngleRev = 0
  Length = 5
  Length2 = 100
  Linearize = true
  Midplane = true
  NewSolid = false
  Placement = pos=(0,0,0) rot=(1,0,0;1.5708rad)
  Profile = -> Sketch010
  Refine = true
  Suppress = false
  Type = 1
FEATURE [PartDesign::Pocket] Pocket003
  BaseFeature = -> Pocket002
  ClaimChildren = false
  Fit = 0
  FitJoin = 0
  InnerFit = 0
  InnerFitJoin = 0
  InnerTaperAngle = 0
  InnerTaperAngleRev = 0
  Length = 9
  Length2 = 100
  Linearize = true
  NewSolid = false
  Placement = pos=(0,0,0) rot=(1,0,0;1.5708rad)
  Profile = -> Sketch001
  Refine = true
  Suppress = false
  Type = 0
FEATURE [PartDesign::Body] Body  label="HGH20CA"
  AutoGroupSolids = false
  ExportMode = 0
  Group = -> [Sketch,Pad,Sketch001,Sketch002,Pad001,Sketch003,Pocket,Sketch004,Pocket001,Mirrored,Sketch010,Pocket002,Pocket003]
  Origin = -> Origin
  Tip = -> Pocket003
  _ExportChildren = -> [Pad,Pad001,Pocket,Pocket001,Mirrored,Pocket002,Pocket003]
  _GroupVersion = 1
FEATURE [App::DocumentObjectGroup] Group  label="Components"
  ExportMode = 1
  Group = -> [Body,Body001]
  _GroupVersion = 1
FEATURE [Part::FeaturePython] Assembly  label="HGH20CA-L-Assembly"  # WARN: FeaturePython — macro-defined, semantics opaque (R4)
  AutoRelax = true
  BuildShape = 0
  Freeze = false
  Group = -> [Constraints,Elements,Parts]
  Placement = pos=(0,54,-7.15256e-07) rot=(0,0,1;0rad)
  Verbose = false
  _LinkVersion = 1
  _SolverType = 1
  _Version = 1
FEATURE [App::FeaturePython] Constraints  # WARN: FeaturePython — macro-defined, semantics opaque (R4)
  Group = -> [Constraint,Constraint001,Constraint002]
  _LinkVersion = 1
  _Version = 1
FEATURE [App::FeaturePython] Elements  # WARN: FeaturePython — macro-defined, semantics opaque (R4)
  Group = -> [_Element,_Element001,_Element002,_Element003,_Element004,Element004]
  _LinkVersion = 1
FEATURE [App::FeaturePython] Constraint  label="Locked"  # WARN: FeaturePython — macro-defined, semantics opaque (R4)
  Disabled = false
  Group = -> [ElementLink]
  _ConstraintType = 0
  _LinkVersion = 1
  _Parent = -> Constraints
FEATURE [App::FeaturePython] ElementLink  label="_Element"  # link proxy (typed FeaturePython)
  LinkTransform = true
  LinkedObject = -> _Element
  _LinkVersion = 1
  _Parent = -> Constraint
FEATURE [Part::FeaturePython] _Element  # link proxy (typed FeaturePython)
  Detach = false
  LinkTransform = true
  LinkedObject = -> Link001 [Pocket003.Face62]
  _LinkVersion = 1
  _Parent = -> Elements
FEATURE [App::FeaturePython] Constraint001  label="Attachment"  # WARN: FeaturePython — macro-defined, semantics opaque (R4)
  Cascade = false
  Disabled = false
  Group = -> [ElementLink001,ElementLink002]
  Multiply = false
  _ConstraintType = 45
  _LinkVersion = 1
  _Parent = -> Constraints
FEATURE [App::FeaturePython] ElementLink001  label="_Element001"  # link proxy (typed FeaturePython)
  LinkTransform = true
  LinkedObject = -> _Element001
  Offset = pos=(0,0,0) rot=(0,0,1;1.8326rad)
  Placement = pos=(23.2788,-2.84e-14,30.3375) rot=(0,-1,0;1.8326rad)
  _LinkVersion = 1
  _Parent = -> Constraint001
FEATURE [Part::FeaturePython] _Element001  # link proxy (typed FeaturePython)
  Detach = false
  LinkTransform = true
  LinkedObject = -> Link002 [Revolution.Edge59]
  _LinkVersion = 1
  _Parent = -> Elements
FEATURE [App::FeaturePython] ElementLink002  label="_Element002"  # link proxy (typed FeaturePython)
  LinkTransform = true
  LinkedObject = -> _Element002
  _LinkVersion = 1
  _Parent = -> Constraint001
FEATURE [Part::FeaturePython] _Element002  # link proxy (typed FeaturePython)
  Detach = false
  LinkTransform = true
  LinkedObject = -> Link001 [Pocket003.Edge186]
  _LinkVersion = 1
  _Parent = -> Elements
FEATURE [App::FeaturePython] Constraint002  label="Attachment001"  # WARN: FeaturePython — macro-defined, semantics opaque (R4)
  Cascade = false
  Disabled = false
  Group = -> [ElementLink003,ElementLink004]
  Multiply = false
  _ConstraintType = 45
  _LinkVersion = 1
  _Parent = -> Constraints
FEATURE [App::FeaturePython] ElementLink003  label="_Element003"  # link proxy (typed FeaturePython)
  LinkTransform = true
  LinkedObject = -> _Element003
  _LinkVersion = 1
  _Parent = -> Constraint002
FEATURE [Part::FeaturePython] _Element003  # link proxy (typed FeaturePython)
  Detach = false
  LinkTransform = true
  LinkedObject = -> Screw [Edge4]
  _LinkVersion = 1
  _Parent = -> Elements
FEATURE [App::FeaturePython] ElementLink004  label="_Element004"  # link proxy (typed FeaturePython)
  LinkTransform = true
  LinkedObject = -> _Element004
  _LinkVersion = 1
  _Parent = -> Constraint002
FEATURE [Part::FeaturePython] _Element004  # link proxy (typed FeaturePython)
  Detach = false
  LinkTransform = true
  LinkedObject = -> Link001 [Pocket003.Edge234]
  _LinkVersion = 1
  _Parent = -> Elements
FEATURE [Part::FeaturePython] Assembly001  label="HGH20CA-R-Assembly"  # WARN: FeaturePython — macro-defined, semantics opaque (R4)
  AutoRelax = true
  BuildShape = 0
  Freeze = false
  Group = -> [Constraints001,Elements001,Parts001]
  Placement = pos=(0,-36,-7.15256e-07) rot=(0,0,1;0rad)
  Verbose = false
  _LinkVersion = 1
  _SolverType = 1
  _Version = 1
FEATURE [App::FeaturePython] Constraints001  # WARN: FeaturePython — macro-defined, semantics opaque (R4)
  Group = -> [Constraint003,Constraint004,Constraint005]
  _LinkVersion = 1
  _Version = 1
FEATURE [App::FeaturePython] Elements001  # WARN: FeaturePython — macro-defined, semantics opaque (R4)
  Group = -> [_Element005,_Element006,_Element007,_Element008,_Element009,Element,Element001,Element002,Element003]
  _LinkVersion = 1
FEATURE [App::FeaturePython] Constraint003  label="Locked001"  # WARN: FeaturePython — macro-defined, semantics opaque (R4)
  Disabled = false
  Group = -> [ElementLink005]
  _ConstraintType = 0
  _LinkVersion = 1
  _Parent = -> Constraints001
FEATURE [App::FeaturePython] ElementLink005  label="_Element005"  # link proxy (typed FeaturePython)
  LinkTransform = true
  LinkedObject = -> _Element005
  _LinkVersion = 1
  _Parent = -> Constraint003
FEATURE [Part::FeaturePython] _Element005  # link proxy (typed FeaturePython)
  Detach = false
  LinkTransform = true
  LinkedObject = -> Link004 [Pocket003.Face62]
  _LinkVersion = 1
  _Parent = -> Elements001
FEATURE [App::FeaturePython] Constraint004  label="Attachment002"  # WARN: FeaturePython — macro-defined, semantics opaque (R4)
  Cascade = false
  Disabled = false
  Group = -> [ElementLink006,ElementLink007]
  Multiply = false
  _ConstraintType = 45
  _LinkVersion = 1
  _Parent = -> Constraints001
FEATURE [App::FeaturePython] ElementLink006  label="_Element006"  # link proxy (typed FeaturePython)
  LinkTransform = true
  LinkedObject = -> _Element006
  Offset = pos=(0,0,0) rot=(1,0,0;3.14159rad)
  Placement = pos=(0,-72.8,48.2) rot=(1,0,0;3.14159rad)
  _LinkVersion = 1
  _Parent = -> Constraint004
FEATURE [Part::FeaturePython] _Element006  # link proxy (typed FeaturePython)
  Detach = false
  LinkTransform = true
  LinkedObject = -> Link004 [Pocket003.Edge234]
  _LinkVersion = 1
  _Parent = -> Elements001
FEATURE [App::FeaturePython] ElementLink007  label="_Element007"  # link proxy (typed FeaturePython)
  LinkTransform = true
  LinkedObject = -> _Element007
  Offset = pos=(0,0,0) rot=(0,0,1;1.309rad)
  Placement = pos=(-23.2788,2.13e-14,17.8625) rot=(0,1,0;1.309rad)
  _LinkVersion = 1
  _Parent = -> Constraint004
FEATURE [Part::FeaturePython] _Element007  # link proxy (typed FeaturePython)
  Detach = false
  LinkTransform = true
  LinkedObject = -> Link003 [Revolution.Edge59]
  _LinkVersion = 1
  _Parent = -> Elements001
FEATURE [App::FeaturePython] Constraint005  label="Attachment003"  # WARN: FeaturePython — macro-defined, semantics opaque (R4)
  Cascade = false
  Disabled = false
  Group = -> [ElementLink008,ElementLink009]
  Multiply = false
  _ConstraintType = 45
  _LinkVersion = 1
  _Parent = -> Constraints001
FEATURE [App::FeaturePython] ElementLink008  label="_Element008"  # link proxy (typed FeaturePython)
  LinkTransform = true
  LinkedObject = -> _Element008
  Offset = pos=(0,0,0) rot=(1,0,0;3.14159rad)
  Placement = pos=(0,72.8,48.2) rot=(1,0,0;3.14159rad)
  _LinkVersion = 1
  _Parent = -> Constraint005
FEATURE [Part::FeaturePython] _Element008  # link proxy (typed FeaturePython)
  Detach = false
  LinkTransform = true
  LinkedObject = -> Link004 [Pocket003.Edge186]
  _LinkVersion = 1
  _Parent = -> Elements001
FEATURE [App::FeaturePython] ElementLink009  label="_Element009"  # link proxy (typed FeaturePython)
  LinkTransform = true
  LinkedObject = -> _Element009
  _LinkVersion = 1
  _Parent = -> Constraint005
FEATURE [Part::FeaturePython] _Element009  # link proxy (typed FeaturePython)
  Detach = false
  LinkTransform = true
  LinkedObject = -> Screw001 [Edge4]
  _LinkVersion = 1
  _Parent = -> Elements001
FEATURE [App::DocumentObjectGroup] Group001  label="Assemblies"
  ExportMode = 1
  Group = -> [Assembly,Assembly001]
  _GroupVersion = 1
FEATURE [Part::FeaturePython] Element  label="top-mate"  # link proxy (typed FeaturePython)
  Detach = false
  LinkTransform = true
  LinkedObject = -> Link004 [Pocket003.Face13]
  _LinkVersion = 1
  _Parent = -> Elements001
FEATURE [Part::FeaturePython] Element001  label="side-mate"  # link proxy (typed FeaturePython)
  Detach = false
  LinkTransform = true
  LinkedObject = -> Link004 [Pocket003.Face17]
  _LinkVersion = 1
  _Parent = -> Elements001
FEATURE [Part::FeaturePython] Element002  label="point"  # link proxy (typed FeaturePython)
  Detach = false
  LinkTransform = true
  LinkedObject = -> Link004 [Pocket003.Vertex56]
  _LinkVersion = 1
  _Parent = -> Elements001
FEATURE [Part::FeaturePython] Element003  label="shim-br"  # link proxy (typed FeaturePython)
  Detach = false
  LinkTransform = true
  LinkedObject = -> Link004 [Pocket003.Edge212]
  _LinkVersion = 1
  _Parent = -> Elements001
FEATURE [Part::FeaturePython] Element004  label="shim-tr"  # link proxy (typed FeaturePython)
  Detach = false
  LinkTransform = true
  LinkedObject = -> Link001 [Pocket003.Edge213]
  _LinkVersion = 1
  _Parent = -> Elements
---- part parts/Spindle.FCStd = doc fcstd_8b07c1d68e44 (89487 chars; too large to inline — full recipe in that document) ----
